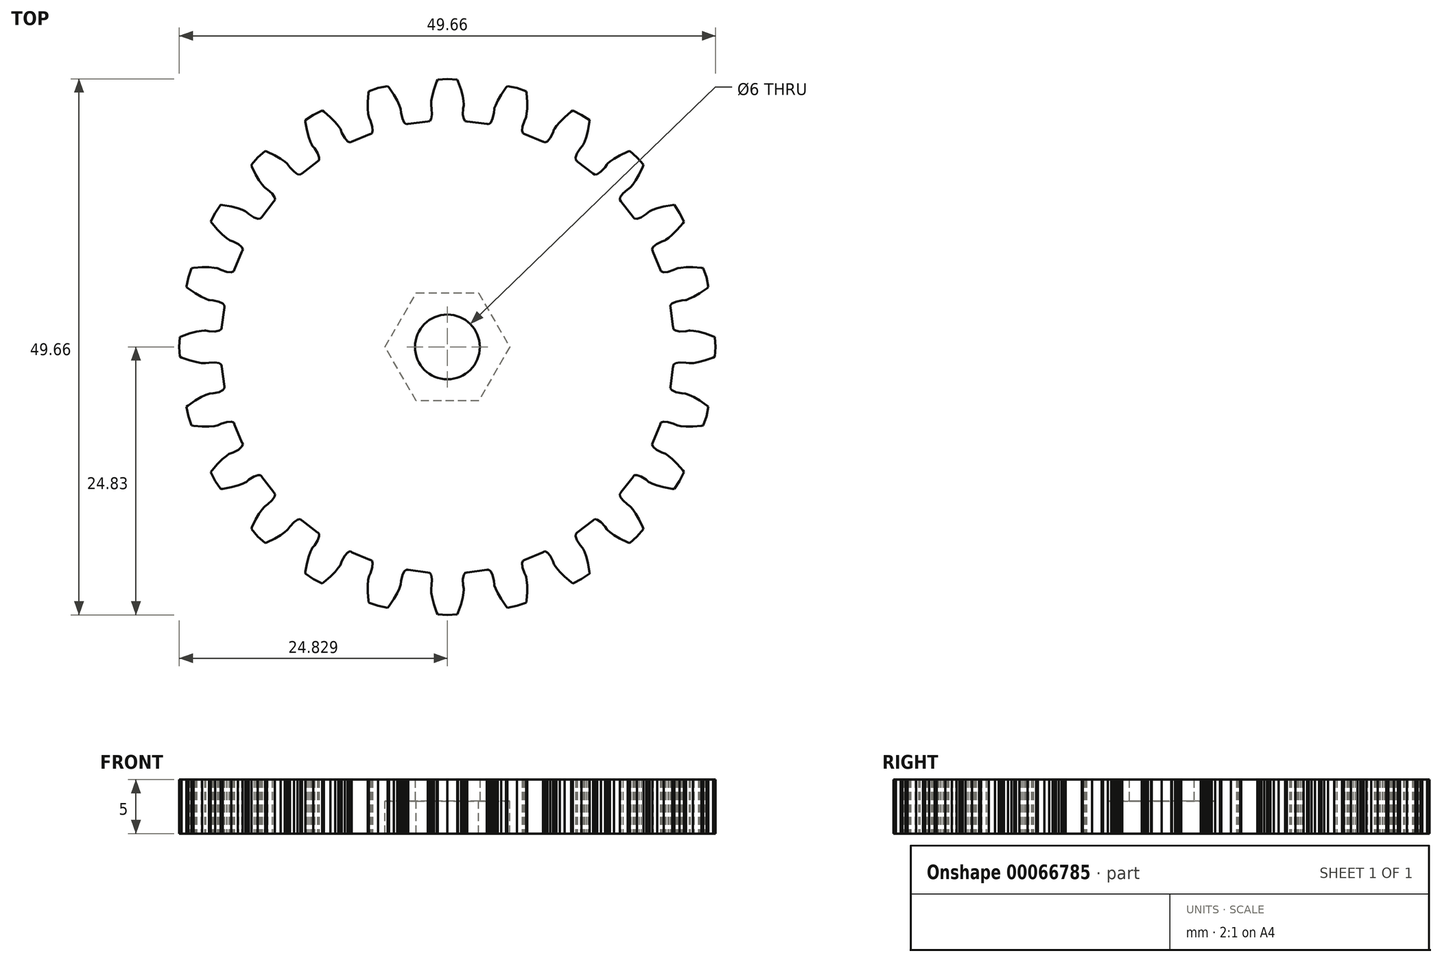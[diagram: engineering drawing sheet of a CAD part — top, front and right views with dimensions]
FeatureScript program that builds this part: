
annotation { "Feature Type Name" : "Feature", "Feature Type Description" : "" }
export const myFeature = defineFeature(function(context is Context, id is Id, definition is map)
    precondition{}
    {
        {
            var Q0;
            Q0=qCreatedBy(makeId("Top.planeOp"),FACE);
            var sketch = newSketch(context, id + "F0", { "sketchPlane" : qUnion([Q0])});
            skLineSegment(sketch, "E0", {"start": v(16.31, -7.28) * mm, "end": v(16.6, -6.43) * mm});
            skLineSegment(sketch, "E1", {"start": v(16.6, -6.43) * mm, "end": v(16.78, -5.54) * mm});
            skLineSegment(sketch, "E2", {"start": v(16.78, -5.54) * mm, "end": v(16.64, -5.42) * mm});
            skLineSegment(sketch, "E3", {"start": v(16.64, -5.42) * mm, "end": v(15.98, -4.96) * mm});
            skLineSegment(sketch, "E4", {"start": v(15.98, -4.96) * mm, "end": v(15.42, -4.65) * mm});
            skLineSegment(sketch, "E5", {"start": v(15.42, -4.65) * mm, "end": v(15, -4.45) * mm});
            skLineSegment(sketch, "E6", {"start": v(15, -4.45) * mm, "end": v(14.73, -4.36) * mm});
            skLineSegment(sketch, "E7", {"start": v(14.73, -4.36) * mm, "end": v(14.63, -4.33) * mm});
            skLineSegment(sketch, "E8", {"start": v(14.63, -4.33) * mm, "end": v(14.33, -4.3) * mm});
            skLineSegment(sketch, "E9", {"start": v(14.33, -4.3) * mm, "end": v(13.78, -4.18) * mm});
            skLineSegment(sketch, "E10", {"start": v(13.78, -4.18) * mm, "end": v(13.42, -4.01) * mm});
            skLineSegment(sketch, "E11", {"start": v(13.42, -4.01) * mm, "end": v(13.25, -3.83) * mm});
            skLineSegment(sketch, "E12", {"start": v(13.25, -3.83) * mm, "end": v(13.28, -3.66) * mm});
            skLineSegment(sketch, "E13", {"start": v(13.28, -3.66) * mm, "end": v(13.28, -3.64) * mm});
            skLineSegment(sketch, "E14", {"start": v(13.28, -3.64) * mm, "end": v(13.52, -1.83) * mm});
            skLineSegment(sketch, "E15", {"start": v(13.52, -1.83) * mm, "end": v(13.52, -1.81) * mm});
            skLineSegment(sketch, "E16", {"start": v(13.52, -1.81) * mm, "end": v(13.54, -1.64) * mm});
            skLineSegment(sketch, "E17", {"start": v(13.54, -1.64) * mm, "end": v(13.75, -1.5) * mm});
            skLineSegment(sketch, "E18", {"start": v(13.75, -1.5) * mm, "end": v(14.14, -1.44) * mm});
            skLineSegment(sketch, "E19", {"start": v(14.14, -1.44) * mm, "end": v(14.7, -1.46) * mm});
            skLineSegment(sketch, "E20", {"start": v(14.7, -1.46) * mm, "end": v(15, -1.51) * mm});
            skLineSegment(sketch, "E21", {"start": v(15, -1.51) * mm, "end": v(15.1, -1.52) * mm});
            skLineSegment(sketch, "E22", {"start": v(15.1, -1.52) * mm, "end": v(15.4, -1.5) * mm});
            skLineSegment(sketch, "E23", {"start": v(15.4, -1.5) * mm, "end": v(15.85, -1.41) * mm});
            skLineSegment(sketch, "E24", {"start": v(15.85, -1.41) * mm, "end": v(16.46, -1.25) * mm});
            skLineSegment(sketch, "E25", {"start": v(16.46, -1.25) * mm, "end": v(17.22, -0.98) * mm});
            skLineSegment(sketch, "E26", {"start": v(17.22, -0.98) * mm, "end": v(17.39, -0.9) * mm});
            skLineSegment(sketch, "E27", {"start": v(17.39, -0.9) * mm, "end": v(17.45, 0) * mm});
            skLineSegment(sketch, "E28", {"start": v(17.45, 0) * mm, "end": v(17.39, 0.9) * mm});
            skLineSegment(sketch, "E29", {"start": v(17.39, 0.9) * mm, "end": v(17.22, 0.98) * mm});
            skLineSegment(sketch, "E30", {"start": v(17.22, 0.98) * mm, "end": v(16.46, 1.25) * mm});
            skLineSegment(sketch, "E31", {"start": v(16.46, 1.25) * mm, "end": v(15.85, 1.41) * mm});
            skLineSegment(sketch, "E32", {"start": v(15.85, 1.41) * mm, "end": v(15.4, 1.5) * mm});
            skLineSegment(sketch, "E33", {"start": v(15.4, 1.5) * mm, "end": v(15.1, 1.52) * mm});
            skLineSegment(sketch, "E34", {"start": v(15.1, 1.52) * mm, "end": v(15, 1.51) * mm});
            skLineSegment(sketch, "E35", {"start": v(15, 1.51) * mm, "end": v(14.7, 1.46) * mm});
            skLineSegment(sketch, "E36", {"start": v(14.7, 1.46) * mm, "end": v(14.14, 1.44) * mm});
            skLineSegment(sketch, "E37", {"start": v(14.14, 1.44) * mm, "end": v(13.75, 1.5) * mm});
            skLineSegment(sketch, "E38", {"start": v(13.75, 1.5) * mm, "end": v(13.54, 1.64) * mm});
            skLineSegment(sketch, "E39", {"start": v(13.54, 1.64) * mm, "end": v(13.52, 1.81) * mm});
            skLineSegment(sketch, "E40", {"start": v(13.52, 1.81) * mm, "end": v(13.52, 1.83) * mm});
            skLineSegment(sketch, "E41", {"start": v(13.52, 1.83) * mm, "end": v(13.28, 3.64) * mm});
            skLineSegment(sketch, "E42", {"start": v(13.28, 3.64) * mm, "end": v(13.28, 3.66) * mm});
            skLineSegment(sketch, "E43", {"start": v(13.28, 3.66) * mm, "end": v(13.25, 3.83) * mm});
            skLineSegment(sketch, "E44", {"start": v(13.25, 3.83) * mm, "end": v(13.42, 4.01) * mm});
            skLineSegment(sketch, "E45", {"start": v(13.42, 4.01) * mm, "end": v(13.78, 4.18) * mm});
            skLineSegment(sketch, "E46", {"start": v(13.78, 4.18) * mm, "end": v(14.33, 4.3) * mm});
            skLineSegment(sketch, "E47", {"start": v(14.33, 4.3) * mm, "end": v(14.63, 4.33) * mm});
            skLineSegment(sketch, "E48", {"start": v(14.63, 4.33) * mm, "end": v(14.73, 4.36) * mm});
            skLineSegment(sketch, "E49", {"start": v(14.73, 4.36) * mm, "end": v(15, 4.45) * mm});
            skLineSegment(sketch, "E50", {"start": v(15, 4.45) * mm, "end": v(15.42, 4.65) * mm});
            skLineSegment(sketch, "E51", {"start": v(15.42, 4.65) * mm, "end": v(15.98, 4.96) * mm});
            skLineSegment(sketch, "E52", {"start": v(15.98, 4.96) * mm, "end": v(16.64, 5.42) * mm});
            skLineSegment(sketch, "E53", {"start": v(16.64, 5.42) * mm, "end": v(16.78, 5.54) * mm});
            skLineSegment(sketch, "E54", {"start": v(16.78, 5.54) * mm, "end": v(16.6, 6.43) * mm});
            skLineSegment(sketch, "E55", {"start": v(16.6, 6.43) * mm, "end": v(16.31, 7.28) * mm});
            skLineSegment(sketch, "E56", {"start": v(16.31, 7.28) * mm, "end": v(16.13, 7.31) * mm});
            skLineSegment(sketch, "E57", {"start": v(16.13, 7.31) * mm, "end": v(15.33, 7.38) * mm});
            skLineSegment(sketch, "E58", {"start": v(15.33, 7.38) * mm, "end": v(14.7, 7.38) * mm});
            skLineSegment(sketch, "E59", {"start": v(14.7, 7.38) * mm, "end": v(14.23, 7.33) * mm});
            skLineSegment(sketch, "E60", {"start": v(14.23, 7.33) * mm, "end": v(13.94, 7.28) * mm});
            skLineSegment(sketch, "E61", {"start": v(13.94, 7.28) * mm, "end": v(13.85, 7.26) * mm});
            skLineSegment(sketch, "E62", {"start": v(13.85, 7.26) * mm, "end": v(13.57, 7.12) * mm});
            skLineSegment(sketch, "E63", {"start": v(13.57, 7.12) * mm, "end": v(13.04, 6.96) * mm});
            skLineSegment(sketch, "E64", {"start": v(13.04, 6.96) * mm, "end": v(12.64, 6.93) * mm});
            skLineSegment(sketch, "E65", {"start": v(12.64, 6.93) * mm, "end": v(12.4, 7) * mm});
            skLineSegment(sketch, "E66", {"start": v(12.4, 7) * mm, "end": v(12.34, 7.16) * mm});
            skLineSegment(sketch, "E67", {"start": v(12.34, 7.16) * mm, "end": v(12.33, 7.18) * mm});
            skLineSegment(sketch, "E68", {"start": v(12.33, 7.18) * mm, "end": v(11.63, 8.87) * mm});
            skLineSegment(sketch, "E69", {"start": v(11.63, 8.87) * mm, "end": v(11.62, 8.88) * mm});
            skLineSegment(sketch, "E70", {"start": v(11.62, 8.88) * mm, "end": v(11.56, 9.04) * mm});
            skLineSegment(sketch, "E71", {"start": v(11.56, 9.04) * mm, "end": v(11.67, 9.26) * mm});
            skLineSegment(sketch, "E72", {"start": v(11.67, 9.26) * mm, "end": v(11.98, 9.52) * mm});
            skLineSegment(sketch, "E73", {"start": v(11.98, 9.52) * mm, "end": v(12.47, 9.78) * mm});
            skLineSegment(sketch, "E74", {"start": v(12.47, 9.78) * mm, "end": v(12.76, 9.88) * mm});
            skLineSegment(sketch, "E75", {"start": v(12.76, 9.88) * mm, "end": v(12.85, 9.93) * mm});
            skLineSegment(sketch, "E76", {"start": v(12.85, 9.93) * mm, "end": v(13.09, 10.1) * mm});
            skLineSegment(sketch, "E77", {"start": v(13.09, 10.1) * mm, "end": v(13.44, 10.4) * mm});
            skLineSegment(sketch, "E78", {"start": v(13.44, 10.4) * mm, "end": v(13.9, 10.84) * mm});
            skLineSegment(sketch, "E79", {"start": v(13.9, 10.84) * mm, "end": v(14.42, 11.45) * mm});
            skLineSegment(sketch, "E80", {"start": v(14.42, 11.45) * mm, "end": v(14.52, 11.6) * mm});
            skLineSegment(sketch, "E81", {"start": v(14.52, 11.6) * mm, "end": v(14.12, 12.41) * mm});
            skLineSegment(sketch, "E82", {"start": v(14.12, 12.41) * mm, "end": v(13.62, 13.17) * mm});
            skLineSegment(sketch, "E83", {"start": v(13.62, 13.17) * mm, "end": v(13.44, 13.15) * mm});
            skLineSegment(sketch, "E84", {"start": v(13.44, 13.15) * mm, "end": v(12.64, 13) * mm});
            skLineSegment(sketch, "E85", {"start": v(12.64, 13) * mm, "end": v(12.03, 12.84) * mm});
            skLineSegment(sketch, "E86", {"start": v(12.03, 12.84) * mm, "end": v(11.6, 12.68) * mm});
            skLineSegment(sketch, "E87", {"start": v(11.6, 12.68) * mm, "end": v(11.33, 12.55) * mm});
            skLineSegment(sketch, "E88", {"start": v(11.33, 12.55) * mm, "end": v(11.25, 12.5) * mm});
            skLineSegment(sketch, "E89", {"start": v(11.25, 12.5) * mm, "end": v(11.01, 12.3) * mm});
            skLineSegment(sketch, "E90", {"start": v(11.01, 12.3) * mm, "end": v(10.54, 12) * mm});
            skLineSegment(sketch, "E91", {"start": v(10.54, 12) * mm, "end": v(10.17, 11.87) * mm});
            skLineSegment(sketch, "E92", {"start": v(10.17, 11.87) * mm, "end": v(9.92, 11.88) * mm});
            skLineSegment(sketch, "E93", {"start": v(9.92, 11.88) * mm, "end": v(9.81, 12.02) * mm});
            skLineSegment(sketch, "E94", {"start": v(9.81, 12.02) * mm, "end": v(9.8, 12.03) * mm});
            skLineSegment(sketch, "E95", {"start": v(9.8, 12.03) * mm, "end": v(8.69, 13.48) * mm});
            skLineSegment(sketch, "E96", {"start": v(8.69, 13.48) * mm, "end": v(8.68, 13.5) * mm});
            skLineSegment(sketch, "E97", {"start": v(8.68, 13.5) * mm, "end": v(8.58, 13.63) * mm});
            skLineSegment(sketch, "E98", {"start": v(8.58, 13.63) * mm, "end": v(8.63, 13.88) * mm});
            skLineSegment(sketch, "E99", {"start": v(8.63, 13.88) * mm, "end": v(8.85, 14.2) * mm});
            skLineSegment(sketch, "E100", {"start": v(8.85, 14.2) * mm, "end": v(9.26, 14.58) * mm});
            skLineSegment(sketch, "E101", {"start": v(9.26, 14.58) * mm, "end": v(9.52, 14.76) * mm});
            skLineSegment(sketch, "E102", {"start": v(9.52, 14.76) * mm, "end": v(9.59, 14.83) * mm});
            skLineSegment(sketch, "E103", {"start": v(9.59, 14.83) * mm, "end": v(9.78, 15.05) * mm});
            skLineSegment(sketch, "E104", {"start": v(9.78, 15.05) * mm, "end": v(10.05, 15.43) * mm});
            skLineSegment(sketch, "E105", {"start": v(10.05, 15.43) * mm, "end": v(10.37, 15.98) * mm});
            skLineSegment(sketch, "E106", {"start": v(10.37, 15.98) * mm, "end": v(10.7, 16.7) * mm});
            skLineSegment(sketch, "E107", {"start": v(10.7, 16.7) * mm, "end": v(10.77, 16.88) * mm});
            skLineSegment(sketch, "E108", {"start": v(10.77, 16.88) * mm, "end": v(10.18, 17.56) * mm});
            skLineSegment(sketch, "E109", {"start": v(10.18, 17.56) * mm, "end": v(9.5, 18.15) * mm});
            skLineSegment(sketch, "E110", {"start": v(9.5, 18.15) * mm, "end": v(9.32, 18.1) * mm});
            skLineSegment(sketch, "E111", {"start": v(9.32, 18.1) * mm, "end": v(8.6, 17.75) * mm});
            skLineSegment(sketch, "E112", {"start": v(8.6, 17.75) * mm, "end": v(8.05, 17.43) * mm});
            skLineSegment(sketch, "E113", {"start": v(8.05, 17.43) * mm, "end": v(7.67, 17.16) * mm});
            skLineSegment(sketch, "E114", {"start": v(7.67, 17.16) * mm, "end": v(7.44, 16.97) * mm});
            skLineSegment(sketch, "E115", {"start": v(7.44, 16.97) * mm, "end": v(7.38, 16.9) * mm});
            skLineSegment(sketch, "E116", {"start": v(7.38, 16.9) * mm, "end": v(7.2, 16.65) * mm});
            skLineSegment(sketch, "E117", {"start": v(7.2, 16.65) * mm, "end": v(6.82, 16.23) * mm});
            skLineSegment(sketch, "E118", {"start": v(6.82, 16.23) * mm, "end": v(6.5, 16) * mm});
            skLineSegment(sketch, "E119", {"start": v(6.5, 16) * mm, "end": v(6.25, 15.96) * mm});
            skLineSegment(sketch, "E120", {"start": v(6.25, 15.96) * mm, "end": v(6.12, 16.06) * mm});
            skLineSegment(sketch, "E121", {"start": v(6.12, 16.06) * mm, "end": v(6.1, 16.07) * mm});
            skLineSegment(sketch, "E122", {"start": v(6.1, 16.07) * mm, "end": v(4.65, 17.18) * mm});
            skLineSegment(sketch, "E123", {"start": v(4.65, 17.18) * mm, "end": v(4.64, 17.2) * mm});
            skLineSegment(sketch, "E124", {"start": v(4.64, 17.2) * mm, "end": v(4.5, 17.3) * mm});
            skLineSegment(sketch, "E125", {"start": v(4.5, 17.3) * mm, "end": v(4.5, 17.55) * mm});
            skLineSegment(sketch, "E126", {"start": v(4.5, 17.55) * mm, "end": v(4.62, 17.92) * mm});
            skLineSegment(sketch, "E127", {"start": v(4.62, 17.92) * mm, "end": v(4.92, 18.4) * mm});
            skLineSegment(sketch, "E128", {"start": v(4.92, 18.4) * mm, "end": v(5.12, 18.63) * mm});
            skLineSegment(sketch, "E129", {"start": v(5.12, 18.63) * mm, "end": v(5.17, 18.71) * mm});
            skLineSegment(sketch, "E130", {"start": v(5.17, 18.71) * mm, "end": v(5.3, 18.98) * mm});
            skLineSegment(sketch, "E131", {"start": v(5.3, 18.98) * mm, "end": v(5.46, 19.41) * mm});
            skLineSegment(sketch, "E132", {"start": v(5.46, 19.41) * mm, "end": v(5.63, 20.02) * mm});
            skLineSegment(sketch, "E133", {"start": v(5.63, 20.02) * mm, "end": v(5.77, 20.82) * mm});
            skLineSegment(sketch, "E134", {"start": v(5.77, 20.82) * mm, "end": v(5.79, 21) * mm});
            skLineSegment(sketch, "E135", {"start": v(5.79, 21) * mm, "end": v(5.03, 21.5) * mm});
            skLineSegment(sketch, "E136", {"start": v(5.03, 21.5) * mm, "end": v(4.22, 21.9) * mm});
            skLineSegment(sketch, "E137", {"start": v(4.22, 21.9) * mm, "end": v(4.07, 21.8) * mm});
            skLineSegment(sketch, "E138", {"start": v(4.07, 21.8) * mm, "end": v(3.46, 21.28) * mm});
            skLineSegment(sketch, "E139", {"start": v(3.46, 21.28) * mm, "end": v(3.01, 20.83) * mm});
            skLineSegment(sketch, "E140", {"start": v(3.01, 20.83) * mm, "end": v(2.71, 20.47) * mm});
            skLineSegment(sketch, "E141", {"start": v(2.71, 20.47) * mm, "end": v(2.55, 20.23) * mm});
            skLineSegment(sketch, "E142", {"start": v(2.55, 20.23) * mm, "end": v(2.5, 20.14) * mm});
            skLineSegment(sketch, "E143", {"start": v(2.5, 20.14) * mm, "end": v(2.4, 19.85) * mm});
            skLineSegment(sketch, "E144", {"start": v(2.4, 19.85) * mm, "end": v(2.14, 19.36) * mm});
            skLineSegment(sketch, "E145", {"start": v(2.14, 19.36) * mm, "end": v(1.88, 19.06) * mm});
            skLineSegment(sketch, "E146", {"start": v(1.88, 19.06) * mm, "end": v(1.66, 18.94) * mm});
            skLineSegment(sketch, "E147", {"start": v(1.66, 18.94) * mm, "end": v(1.5, 19) * mm});
            skLineSegment(sketch, "E148", {"start": v(1.5, 19) * mm, "end": v(1.48, 19.01) * mm});
            skLineSegment(sketch, "E149", {"start": v(1.48, 19.01) * mm, "end": v(-0.2, 19.71) * mm});
            skLineSegment(sketch, "E150", {"start": v(-0.2, 19.71) * mm, "end": v(-0.22, 19.72) * mm});
            skLineSegment(sketch, "E151", {"start": v(-0.22, 19.72) * mm, "end": v(-0.38, 19.78) * mm});
            skLineSegment(sketch, "E152", {"start": v(-0.38, 19.78) * mm, "end": v(-0.45, 20.02) * mm});
            skLineSegment(sketch, "E153", {"start": v(-0.45, 20.02) * mm, "end": v(-0.42, 20.42) * mm});
            skLineSegment(sketch, "E154", {"start": v(-0.42, 20.42) * mm, "end": v(-0.26, 20.95) * mm});
            skLineSegment(sketch, "E155", {"start": v(-0.26, 20.95) * mm, "end": v(-0.12, 21.23) * mm});
            skLineSegment(sketch, "E156", {"start": v(-0.12, 21.23) * mm, "end": v(-0.1, 21.32) * mm});
            skLineSegment(sketch, "E157", {"start": v(-0.1, 21.32) * mm, "end": v(-0.05, 21.61) * mm});
            skLineSegment(sketch, "E158", {"start": v(-0.05, 21.61) * mm, "end": v(0, 22.07) * mm});
            skLineSegment(sketch, "E159", {"start": v(0, 22.07) * mm, "end": v(0, 22.7) * mm});
            skLineSegment(sketch, "E160", {"start": v(0, 22.7) * mm, "end": v(-0.07, 23.51) * mm});
            skLineSegment(sketch, "E161", {"start": v(-0.07, 23.51) * mm, "end": v(-0.1, 23.7) * mm});
            skLineSegment(sketch, "E162", {"start": v(-0.1, 23.7) * mm, "end": v(-0.95, 23.98) * mm});
            skLineSegment(sketch, "E163", {"start": v(-0.95, 23.98) * mm, "end": v(-1.84, 24.16) * mm});
            skLineSegment(sketch, "E164", {"start": v(-1.84, 24.16) * mm, "end": v(-1.96, 24.02) * mm});
            skLineSegment(sketch, "E165", {"start": v(-1.96, 24.02) * mm, "end": v(-2.42, 23.36) * mm});
            skLineSegment(sketch, "E166", {"start": v(-2.42, 23.36) * mm, "end": v(-2.73, 22.8) * mm});
            skLineSegment(sketch, "E167", {"start": v(-2.73, 22.8) * mm, "end": v(-2.93, 22.38) * mm});
            skLineSegment(sketch, "E168", {"start": v(-2.93, 22.38) * mm, "end": v(-3.03, 22.1) * mm});
            skLineSegment(sketch, "E169", {"start": v(-3.03, 22.1) * mm, "end": v(-3.05, 22.01) * mm});
            skLineSegment(sketch, "E170", {"start": v(-3.05, 22.01) * mm, "end": v(-3.08, 21.7) * mm});
            skLineSegment(sketch, "E171", {"start": v(-3.08, 21.7) * mm, "end": v(-3.2, 21.16) * mm});
            skLineSegment(sketch, "E172", {"start": v(-3.2, 21.16) * mm, "end": v(-3.37, 20.8) * mm});
            skLineSegment(sketch, "E173", {"start": v(-3.37, 20.8) * mm, "end": v(-3.55, 20.64) * mm});
            skLineSegment(sketch, "E174", {"start": v(-3.55, 20.64) * mm, "end": v(-3.72, 20.66) * mm});
            skLineSegment(sketch, "E175", {"start": v(-3.72, 20.66) * mm, "end": v(-3.74, 20.66) * mm});
            skLineSegment(sketch, "E176", {"start": v(-3.74, 20.66) * mm, "end": v(-5.55, 20.9) * mm});
            skLineSegment(sketch, "E177", {"start": v(-5.55, 20.9) * mm, "end": v(-5.57, 20.9) * mm});
            skLineSegment(sketch, "E178", {"start": v(-5.57, 20.9) * mm, "end": v(-5.74, 20.92) * mm});
            skLineSegment(sketch, "E179", {"start": v(-5.74, 20.92) * mm, "end": v(-5.87, 21.13) * mm});
            skLineSegment(sketch, "E180", {"start": v(-5.87, 21.13) * mm, "end": v(-5.94, 21.52) * mm});
            skLineSegment(sketch, "E181", {"start": v(-5.94, 21.52) * mm, "end": v(-5.92, 22.08) * mm});
            skLineSegment(sketch, "E182", {"start": v(-5.92, 22.08) * mm, "end": v(-5.87, 22.38) * mm});
            skLineSegment(sketch, "E183", {"start": v(-5.87, 22.38) * mm, "end": v(-5.87, 22.48) * mm});
            skLineSegment(sketch, "E184", {"start": v(-5.87, 22.48) * mm, "end": v(-5.89, 22.77) * mm});
            skLineSegment(sketch, "E185", {"start": v(-5.89, 22.77) * mm, "end": v(-5.97, 23.23) * mm});
            skLineSegment(sketch, "E186", {"start": v(-5.97, 23.23) * mm, "end": v(-6.13, 23.85) * mm});
            skLineSegment(sketch, "E187", {"start": v(-6.13, 23.85) * mm, "end": v(-6.4, 24.6) * mm});
            skLineSegment(sketch, "E188", {"start": v(-6.4, 24.6) * mm, "end": v(-6.48, 24.77) * mm});
            skLineSegment(sketch, "E189", {"start": v(-6.48, 24.77) * mm, "end": v(-7.38, 24.83) * mm});
            skLineSegment(sketch, "E190", {"start": v(-7.38, 24.83) * mm, "end": v(-8.28, 24.77) * mm});
            skLineSegment(sketch, "E191", {"start": v(-8.28, 24.77) * mm, "end": v(-8.36, 24.6) * mm});
            skLineSegment(sketch, "E192", {"start": v(-8.36, 24.6) * mm, "end": v(-8.63, 23.85) * mm});
            skLineSegment(sketch, "E193", {"start": v(-8.63, 23.85) * mm, "end": v(-8.8, 23.23) * mm});
            skLineSegment(sketch, "E194", {"start": v(-8.8, 23.23) * mm, "end": v(-8.87, 22.77) * mm});
            skLineSegment(sketch, "E195", {"start": v(-8.87, 22.77) * mm, "end": v(-8.9, 22.48) * mm});
            skLineSegment(sketch, "E196", {"start": v(-8.9, 22.48) * mm, "end": v(-8.9, 22.38) * mm});
            skLineSegment(sketch, "E197", {"start": v(-8.9, 22.38) * mm, "end": v(-8.84, 22.08) * mm});
            skLineSegment(sketch, "E198", {"start": v(-8.84, 22.08) * mm, "end": v(-8.82, 21.52) * mm});
            skLineSegment(sketch, "E199", {"start": v(-8.82, 21.52) * mm, "end": v(-8.89, 21.13) * mm});
            skLineSegment(sketch, "E200", {"start": v(-8.89, 21.13) * mm, "end": v(-9.02, 20.92) * mm});
            skLineSegment(sketch, "E201", {"start": v(-9.02, 20.92) * mm, "end": v(-9.2, 20.9) * mm});
            skLineSegment(sketch, "E202", {"start": v(-9.2, 20.9) * mm, "end": v(-9.2, 20.9) * mm});
            skLineSegment(sketch, "E203", {"start": v(-9.2, 20.9) * mm, "end": v(-11.02, 20.66) * mm});
            skLineSegment(sketch, "E204", {"start": v(-11.02, 20.66) * mm, "end": v(-11.04, 20.66) * mm});
            skLineSegment(sketch, "E205", {"start": v(-11.04, 20.66) * mm, "end": v(-11.2, 20.64) * mm});
            skLineSegment(sketch, "E206", {"start": v(-11.2, 20.64) * mm, "end": v(-11.4, 20.8) * mm});
            skLineSegment(sketch, "E207", {"start": v(-11.4, 20.8) * mm, "end": v(-11.56, 21.16) * mm});
            skLineSegment(sketch, "E208", {"start": v(-11.56, 21.16) * mm, "end": v(-11.69, 21.7) * mm});
            skLineSegment(sketch, "E209", {"start": v(-11.69, 21.7) * mm, "end": v(-11.71, 22.01) * mm});
            skLineSegment(sketch, "E210", {"start": v(-11.71, 22.01) * mm, "end": v(-11.74, 22.1) * mm});
            skLineSegment(sketch, "E211", {"start": v(-11.74, 22.1) * mm, "end": v(-11.84, 22.38) * mm});
            skLineSegment(sketch, "E212", {"start": v(-11.84, 22.38) * mm, "end": v(-12.03, 22.8) * mm});
            skLineSegment(sketch, "E213", {"start": v(-12.03, 22.8) * mm, "end": v(-12.34, 23.36) * mm});
            skLineSegment(sketch, "E214", {"start": v(-12.34, 23.36) * mm, "end": v(-12.8, 24.02) * mm});
            skLineSegment(sketch, "E215", {"start": v(-12.8, 24.02) * mm, "end": v(-12.92, 24.16) * mm});
            skLineSegment(sketch, "E216", {"start": v(-12.92, 24.16) * mm, "end": v(-13.8, 23.98) * mm});
            skLineSegment(sketch, "E217", {"start": v(-13.8, 23.98) * mm, "end": v(-14.66, 23.7) * mm});
            skLineSegment(sketch, "E218", {"start": v(-14.66, 23.7) * mm, "end": v(-14.7, 23.51) * mm});
            skLineSegment(sketch, "E219", {"start": v(-14.7, 23.51) * mm, "end": v(-14.76, 22.7) * mm});
            skLineSegment(sketch, "E220", {"start": v(-14.76, 22.7) * mm, "end": v(-14.76, 22.07) * mm});
            skLineSegment(sketch, "E221", {"start": v(-14.76, 22.07) * mm, "end": v(-14.72, 21.61) * mm});
            skLineSegment(sketch, "E222", {"start": v(-14.72, 21.61) * mm, "end": v(-14.66, 21.32) * mm});
            skLineSegment(sketch, "E223", {"start": v(-14.66, 21.32) * mm, "end": v(-14.64, 21.23) * mm});
            skLineSegment(sketch, "E224", {"start": v(-14.64, 21.23) * mm, "end": v(-14.5, 20.95) * mm});
            skLineSegment(sketch, "E225", {"start": v(-14.5, 20.95) * mm, "end": v(-14.34, 20.42) * mm});
            skLineSegment(sketch, "E226", {"start": v(-14.34, 20.42) * mm, "end": v(-14.3, 20.02) * mm});
            skLineSegment(sketch, "E227", {"start": v(-14.3, 20.02) * mm, "end": v(-14.38, 19.78) * mm});
            skLineSegment(sketch, "E228", {"start": v(-14.38, 19.78) * mm, "end": v(-14.54, 19.72) * mm});
            skLineSegment(sketch, "E229", {"start": v(-14.54, 19.72) * mm, "end": v(-14.56, 19.71) * mm});
            skLineSegment(sketch, "E230", {"start": v(-14.56, 19.71) * mm, "end": v(-16.25, 19.01) * mm});
            skLineSegment(sketch, "E231", {"start": v(-16.25, 19.01) * mm, "end": v(-16.26, 19) * mm});
            skLineSegment(sketch, "E232", {"start": v(-16.26, 19) * mm, "end": v(-16.42, 18.94) * mm});
            skLineSegment(sketch, "E233", {"start": v(-16.42, 18.94) * mm, "end": v(-16.64, 19.06) * mm});
            skLineSegment(sketch, "E234", {"start": v(-16.64, 19.06) * mm, "end": v(-16.9, 19.36) * mm});
            skLineSegment(sketch, "E235", {"start": v(-16.9, 19.36) * mm, "end": v(-17.16, 19.85) * mm});
            skLineSegment(sketch, "E236", {"start": v(-17.16, 19.85) * mm, "end": v(-17.26, 20.14) * mm});
            skLineSegment(sketch, "E237", {"start": v(-17.26, 20.14) * mm, "end": v(-17.3, 20.23) * mm});
            skLineSegment(sketch, "E238", {"start": v(-17.3, 20.23) * mm, "end": v(-17.48, 20.47) * mm});
            skLineSegment(sketch, "E239", {"start": v(-17.48, 20.47) * mm, "end": v(-17.77, 20.83) * mm});
            skLineSegment(sketch, "E240", {"start": v(-17.77, 20.83) * mm, "end": v(-18.22, 21.28) * mm});
            skLineSegment(sketch, "E241", {"start": v(-18.22, 21.28) * mm, "end": v(-18.83, 21.8) * mm});
            skLineSegment(sketch, "E242", {"start": v(-18.83, 21.8) * mm, "end": v(-18.98, 21.9) * mm});
            skLineSegment(sketch, "E243", {"start": v(-18.98, 21.9) * mm, "end": v(-19.8, 21.5) * mm});
            skLineSegment(sketch, "E244", {"start": v(-19.8, 21.5) * mm, "end": v(-20.55, 21) * mm});
            skLineSegment(sketch, "E245", {"start": v(-20.55, 21) * mm, "end": v(-20.53, 20.82) * mm});
            skLineSegment(sketch, "E246", {"start": v(-20.53, 20.82) * mm, "end": v(-20.39, 20.02) * mm});
            skLineSegment(sketch, "E247", {"start": v(-20.39, 20.02) * mm, "end": v(-20.22, 19.41) * mm});
            skLineSegment(sketch, "E248", {"start": v(-20.22, 19.41) * mm, "end": v(-20.06, 18.98) * mm});
            skLineSegment(sketch, "E249", {"start": v(-20.06, 18.98) * mm, "end": v(-19.93, 18.71) * mm});
            skLineSegment(sketch, "E250", {"start": v(-19.93, 18.71) * mm, "end": v(-19.88, 18.63) * mm});
            skLineSegment(sketch, "E251", {"start": v(-19.88, 18.63) * mm, "end": v(-19.69, 18.4) * mm});
            skLineSegment(sketch, "E252", {"start": v(-19.69, 18.4) * mm, "end": v(-19.39, 17.92) * mm});
            skLineSegment(sketch, "E253", {"start": v(-19.39, 17.92) * mm, "end": v(-19.25, 17.55) * mm});
            skLineSegment(sketch, "E254", {"start": v(-19.25, 17.55) * mm, "end": v(-19.27, 17.3) * mm});
            skLineSegment(sketch, "E255", {"start": v(-19.27, 17.3) * mm, "end": v(-19.4, 17.2) * mm});
            skLineSegment(sketch, "E256", {"start": v(-19.4, 17.2) * mm, "end": v(-19.41, 17.18) * mm});
            skLineSegment(sketch, "E257", {"start": v(-19.41, 17.18) * mm, "end": v(-20.87, 16.07) * mm});
            skLineSegment(sketch, "E258", {"start": v(-20.87, 16.07) * mm, "end": v(-20.88, 16.06) * mm});
            skLineSegment(sketch, "E259", {"start": v(-20.88, 16.06) * mm, "end": v(-21.01, 15.96) * mm});
            skLineSegment(sketch, "E260", {"start": v(-21.01, 15.96) * mm, "end": v(-21.26, 16) * mm});
            skLineSegment(sketch, "E261", {"start": v(-21.26, 16) * mm, "end": v(-21.58, 16.23) * mm});
            skLineSegment(sketch, "E262", {"start": v(-21.58, 16.23) * mm, "end": v(-21.96, 16.65) * mm});
            skLineSegment(sketch, "E263", {"start": v(-21.96, 16.65) * mm, "end": v(-22.14, 16.9) * mm});
            skLineSegment(sketch, "E264", {"start": v(-22.14, 16.9) * mm, "end": v(-22.2, 16.97) * mm});
            skLineSegment(sketch, "E265", {"start": v(-22.2, 16.97) * mm, "end": v(-22.43, 17.16) * mm});
            skLineSegment(sketch, "E266", {"start": v(-22.43, 17.16) * mm, "end": v(-22.8, 17.43) * mm});
            skLineSegment(sketch, "E267", {"start": v(-22.8, 17.43) * mm, "end": v(-23.36, 17.75) * mm});
            skLineSegment(sketch, "E268", {"start": v(-23.36, 17.75) * mm, "end": v(-24.09, 18.1) * mm});
            skLineSegment(sketch, "E269", {"start": v(-24.09, 18.1) * mm, "end": v(-24.26, 18.15) * mm});
            skLineSegment(sketch, "E270", {"start": v(-24.26, 18.15) * mm, "end": v(-24.94, 17.56) * mm});
            skLineSegment(sketch, "E271", {"start": v(-24.94, 17.56) * mm, "end": v(-25.53, 16.88) * mm});
            skLineSegment(sketch, "E272", {"start": v(-25.53, 16.88) * mm, "end": v(-25.47, 16.7) * mm});
            skLineSegment(sketch, "E273", {"start": v(-25.47, 16.7) * mm, "end": v(-25.13, 15.98) * mm});
            skLineSegment(sketch, "E274", {"start": v(-25.13, 15.98) * mm, "end": v(-24.8, 15.43) * mm});
            skLineSegment(sketch, "E275", {"start": v(-24.8, 15.43) * mm, "end": v(-24.54, 15.05) * mm});
            skLineSegment(sketch, "E276", {"start": v(-24.54, 15.05) * mm, "end": v(-24.35, 14.83) * mm});
            skLineSegment(sketch, "E277", {"start": v(-24.35, 14.83) * mm, "end": v(-24.28, 14.76) * mm});
            skLineSegment(sketch, "E278", {"start": v(-24.28, 14.76) * mm, "end": v(-24.03, 14.58) * mm});
            skLineSegment(sketch, "E279", {"start": v(-24.03, 14.58) * mm, "end": v(-23.62, 14.2) * mm});
            skLineSegment(sketch, "E280", {"start": v(-23.62, 14.2) * mm, "end": v(-23.4, 13.88) * mm});
            skLineSegment(sketch, "E281", {"start": v(-23.4, 13.88) * mm, "end": v(-23.34, 13.63) * mm});
            skLineSegment(sketch, "E282", {"start": v(-23.34, 13.63) * mm, "end": v(-23.44, 13.5) * mm});
            skLineSegment(sketch, "E283", {"start": v(-23.44, 13.5) * mm, "end": v(-23.45, 13.48) * mm});
            skLineSegment(sketch, "E284", {"start": v(-23.45, 13.48) * mm, "end": v(-24.57, 12.03) * mm});
            skLineSegment(sketch, "E285", {"start": v(-24.57, 12.03) * mm, "end": v(-24.57, 12.02) * mm});
            skLineSegment(sketch, "E286", {"start": v(-24.57, 12.02) * mm, "end": v(-24.68, 11.88) * mm});
            skLineSegment(sketch, "E287", {"start": v(-24.68, 11.88) * mm, "end": v(-24.93, 11.87) * mm});
            skLineSegment(sketch, "E288", {"start": v(-24.93, 11.87) * mm, "end": v(-25.3, 12) * mm});
            skLineSegment(sketch, "E289", {"start": v(-25.3, 12) * mm, "end": v(-25.77, 12.3) * mm});
            skLineSegment(sketch, "E290", {"start": v(-25.77, 12.3) * mm, "end": v(-26, 12.5) * mm});
            skLineSegment(sketch, "E291", {"start": v(-26, 12.5) * mm, "end": v(-26.1, 12.55) * mm});
            skLineSegment(sketch, "E292", {"start": v(-26.1, 12.55) * mm, "end": v(-26.36, 12.68) * mm});
            skLineSegment(sketch, "E293", {"start": v(-26.36, 12.68) * mm, "end": v(-26.8, 12.84) * mm});
            skLineSegment(sketch, "E294", {"start": v(-26.8, 12.84) * mm, "end": v(-27.4, 13) * mm});
            skLineSegment(sketch, "E295", {"start": v(-27.4, 13) * mm, "end": v(-28.2, 13.15) * mm});
            skLineSegment(sketch, "E296", {"start": v(-28.2, 13.15) * mm, "end": v(-28.38, 13.17) * mm});
            skLineSegment(sketch, "E297", {"start": v(-28.38, 13.17) * mm, "end": v(-28.88, 12.41) * mm});
            skLineSegment(sketch, "E298", {"start": v(-28.88, 12.41) * mm, "end": v(-29.28, 11.6) * mm});
            skLineSegment(sketch, "E299", {"start": v(-29.28, 11.6) * mm, "end": v(-29.18, 11.45) * mm});
            skLineSegment(sketch, "E300", {"start": v(-29.18, 11.45) * mm, "end": v(-28.66, 10.84) * mm});
            skLineSegment(sketch, "E301", {"start": v(-28.66, 10.84) * mm, "end": v(-28.2, 10.4) * mm});
            skLineSegment(sketch, "E302", {"start": v(-28.2, 10.4) * mm, "end": v(-27.85, 10.1) * mm});
            skLineSegment(sketch, "E303", {"start": v(-27.85, 10.1) * mm, "end": v(-27.6, 9.93) * mm});
            skLineSegment(sketch, "E304", {"start": v(-27.6, 9.93) * mm, "end": v(-27.52, 9.88) * mm});
            skLineSegment(sketch, "E305", {"start": v(-27.52, 9.88) * mm, "end": v(-27.23, 9.78) * mm});
            skLineSegment(sketch, "E306", {"start": v(-27.23, 9.78) * mm, "end": v(-26.74, 9.52) * mm});
            skLineSegment(sketch, "E307", {"start": v(-26.74, 9.52) * mm, "end": v(-26.44, 9.26) * mm});
            skLineSegment(sketch, "E308", {"start": v(-26.44, 9.26) * mm, "end": v(-26.32, 9.04) * mm});
            skLineSegment(sketch, "E309", {"start": v(-26.32, 9.04) * mm, "end": v(-26.39, 8.88) * mm});
            skLineSegment(sketch, "E310", {"start": v(-26.39, 8.88) * mm, "end": v(-26.4, 8.87) * mm});
            skLineSegment(sketch, "E311", {"start": v(-26.4, 8.87) * mm, "end": v(-27.1, 7.18) * mm});
            skLineSegment(sketch, "E312", {"start": v(-27.1, 7.18) * mm, "end": v(-27.1, 7.16) * mm});
            skLineSegment(sketch, "E313", {"start": v(-27.1, 7.16) * mm, "end": v(-27.17, 7) * mm});
            skLineSegment(sketch, "E314", {"start": v(-27.17, 7) * mm, "end": v(-27.4, 6.93) * mm});
            skLineSegment(sketch, "E315", {"start": v(-27.4, 6.93) * mm, "end": v(-27.8, 6.96) * mm});
            skLineSegment(sketch, "E316", {"start": v(-27.8, 6.96) * mm, "end": v(-28.33, 7.12) * mm});
            skLineSegment(sketch, "E317", {"start": v(-28.33, 7.12) * mm, "end": v(-28.61, 7.26) * mm});
            skLineSegment(sketch, "E318", {"start": v(-28.61, 7.26) * mm, "end": v(-28.7, 7.28) * mm});
            skLineSegment(sketch, "E319", {"start": v(-28.7, 7.28) * mm, "end": v(-29, 7.33) * mm});
            skLineSegment(sketch, "E320", {"start": v(-29, 7.33) * mm, "end": v(-29.46, 7.38) * mm});
            skLineSegment(sketch, "E321", {"start": v(-29.46, 7.38) * mm, "end": v(-30.09, 7.38) * mm});
            skLineSegment(sketch, "E322", {"start": v(-30.09, 7.38) * mm, "end": v(-30.9, 7.31) * mm});
            skLineSegment(sketch, "E323", {"start": v(-30.9, 7.31) * mm, "end": v(-31.07, 7.28) * mm});
            skLineSegment(sketch, "E324", {"start": v(-31.07, 7.28) * mm, "end": v(-31.36, 6.43) * mm});
            skLineSegment(sketch, "E325", {"start": v(-31.36, 6.43) * mm, "end": v(-31.54, 5.54) * mm});
            skLineSegment(sketch, "E326", {"start": v(-31.54, 5.54) * mm, "end": v(-31.4, 5.42) * mm});
            skLineSegment(sketch, "E327", {"start": v(-31.4, 5.42) * mm, "end": v(-30.74, 4.96) * mm});
            skLineSegment(sketch, "E328", {"start": v(-30.74, 4.96) * mm, "end": v(-30.19, 4.65) * mm});
            skLineSegment(sketch, "E329", {"start": v(-30.19, 4.65) * mm, "end": v(-29.77, 4.45) * mm});
            skLineSegment(sketch, "E330", {"start": v(-29.77, 4.45) * mm, "end": v(-29.49, 4.36) * mm});
            skLineSegment(sketch, "E331", {"start": v(-29.49, 4.36) * mm, "end": v(-29.4, 4.33) * mm});
            skLineSegment(sketch, "E332", {"start": v(-29.4, 4.33) * mm, "end": v(-29.09, 4.3) * mm});
            skLineSegment(sketch, "E333", {"start": v(-29.09, 4.3) * mm, "end": v(-28.54, 4.18) * mm});
            skLineSegment(sketch, "E334", {"start": v(-28.54, 4.18) * mm, "end": v(-28.18, 4.01) * mm});
            skLineSegment(sketch, "E335", {"start": v(-28.18, 4.01) * mm, "end": v(-28.02, 3.83) * mm});
            skLineSegment(sketch, "E336", {"start": v(-28.02, 3.83) * mm, "end": v(-28.04, 3.66) * mm});
            skLineSegment(sketch, "E337", {"start": v(-28.04, 3.66) * mm, "end": v(-28.04, 3.64) * mm});
            skLineSegment(sketch, "E338", {"start": v(-28.04, 3.64) * mm, "end": v(-28.28, 1.83) * mm});
            skLineSegment(sketch, "E339", {"start": v(-28.28, 1.83) * mm, "end": v(-28.28, 1.81) * mm});
            skLineSegment(sketch, "E340", {"start": v(-28.28, 1.81) * mm, "end": v(-28.3, 1.64) * mm});
            skLineSegment(sketch, "E341", {"start": v(-28.3, 1.64) * mm, "end": v(-28.51, 1.5) * mm});
            skLineSegment(sketch, "E342", {"start": v(-28.51, 1.5) * mm, "end": v(-28.9, 1.44) * mm});
            skLineSegment(sketch, "E343", {"start": v(-28.9, 1.44) * mm, "end": v(-29.46, 1.46) * mm});
            skLineSegment(sketch, "E344", {"start": v(-29.46, 1.46) * mm, "end": v(-29.76, 1.51) * mm});
            skLineSegment(sketch, "E345", {"start": v(-29.76, 1.51) * mm, "end": v(-29.86, 1.52) * mm});
            skLineSegment(sketch, "E346", {"start": v(-29.86, 1.52) * mm, "end": v(-30.16, 1.5) * mm});
            skLineSegment(sketch, "E347", {"start": v(-30.16, 1.5) * mm, "end": v(-30.61, 1.41) * mm});
            skLineSegment(sketch, "E348", {"start": v(-30.61, 1.41) * mm, "end": v(-31.23, 1.25) * mm});
            skLineSegment(sketch, "E349", {"start": v(-31.23, 1.25) * mm, "end": v(-31.98, 0.98) * mm});
            skLineSegment(sketch, "E350", {"start": v(-31.98, 0.98) * mm, "end": v(-32.15, 0.9) * mm});
            skLineSegment(sketch, "E351", {"start": v(-32.15, 0.9) * mm, "end": v(-32.2, 0) * mm});
            skLineSegment(sketch, "E352", {"start": v(-32.2, 0) * mm, "end": v(-32.15, -0.9) * mm});
            skLineSegment(sketch, "E353", {"start": v(-32.15, -0.9) * mm, "end": v(-31.98, -0.98) * mm});
            skLineSegment(sketch, "E354", {"start": v(-31.98, -0.98) * mm, "end": v(-31.23, -1.25) * mm});
            skLineSegment(sketch, "E355", {"start": v(-31.23, -1.25) * mm, "end": v(-30.61, -1.41) * mm});
            skLineSegment(sketch, "E356", {"start": v(-30.61, -1.41) * mm, "end": v(-30.16, -1.5) * mm});
            skLineSegment(sketch, "E357", {"start": v(-30.16, -1.5) * mm, "end": v(-29.86, -1.52) * mm});
            skLineSegment(sketch, "E358", {"start": v(-29.86, -1.52) * mm, "end": v(-29.76, -1.51) * mm});
            skLineSegment(sketch, "E359", {"start": v(-29.76, -1.51) * mm, "end": v(-29.46, -1.46) * mm});
            skLineSegment(sketch, "E360", {"start": v(-29.46, -1.46) * mm, "end": v(-28.9, -1.44) * mm});
            skLineSegment(sketch, "E361", {"start": v(-28.9, -1.44) * mm, "end": v(-28.51, -1.5) * mm});
            skLineSegment(sketch, "E362", {"start": v(-28.51, -1.5) * mm, "end": v(-28.3, -1.64) * mm});
            skLineSegment(sketch, "E363", {"start": v(-28.3, -1.64) * mm, "end": v(-28.28, -1.81) * mm});
            skLineSegment(sketch, "E364", {"start": v(-28.28, -1.81) * mm, "end": v(-28.28, -1.83) * mm});
            skLineSegment(sketch, "E365", {"start": v(-28.28, -1.83) * mm, "end": v(-28.04, -3.64) * mm});
            skLineSegment(sketch, "E366", {"start": v(-28.04, -3.64) * mm, "end": v(-28.04, -3.66) * mm});
            skLineSegment(sketch, "E367", {"start": v(-28.04, -3.66) * mm, "end": v(-28.02, -3.83) * mm});
            skLineSegment(sketch, "E368", {"start": v(-28.02, -3.83) * mm, "end": v(-28.18, -4.01) * mm});
            skLineSegment(sketch, "E369", {"start": v(-28.18, -4.01) * mm, "end": v(-28.54, -4.18) * mm});
            skLineSegment(sketch, "E370", {"start": v(-28.54, -4.18) * mm, "end": v(-29.09, -4.3) * mm});
            skLineSegment(sketch, "E371", {"start": v(-29.09, -4.3) * mm, "end": v(-29.4, -4.33) * mm});
            skLineSegment(sketch, "E372", {"start": v(-29.4, -4.33) * mm, "end": v(-29.49, -4.36) * mm});
            skLineSegment(sketch, "E373", {"start": v(-29.49, -4.36) * mm, "end": v(-29.77, -4.45) * mm});
            skLineSegment(sketch, "E374", {"start": v(-29.77, -4.45) * mm, "end": v(-30.19, -4.65) * mm});
            skLineSegment(sketch, "E375", {"start": v(-30.19, -4.65) * mm, "end": v(-30.74, -4.96) * mm});
            skLineSegment(sketch, "E376", {"start": v(-30.74, -4.96) * mm, "end": v(-31.4, -5.42) * mm});
            skLineSegment(sketch, "E377", {"start": v(-31.4, -5.42) * mm, "end": v(-31.54, -5.54) * mm});
            skLineSegment(sketch, "E378", {"start": v(-31.54, -5.54) * mm, "end": v(-31.36, -6.43) * mm});
            skLineSegment(sketch, "E379", {"start": v(-31.36, -6.43) * mm, "end": v(-31.07, -7.28) * mm});
            skLineSegment(sketch, "E380", {"start": v(-31.07, -7.28) * mm, "end": v(-30.9, -7.31) * mm});
            skLineSegment(sketch, "E381", {"start": v(-30.9, -7.31) * mm, "end": v(-30.09, -7.38) * mm});
            skLineSegment(sketch, "E382", {"start": v(-30.09, -7.38) * mm, "end": v(-29.46, -7.38) * mm});
            skLineSegment(sketch, "E383", {"start": v(-29.46, -7.38) * mm, "end": v(-29, -7.33) * mm});
            skLineSegment(sketch, "E384", {"start": v(-29, -7.33) * mm, "end": v(-28.7, -7.28) * mm});
            skLineSegment(sketch, "E385", {"start": v(-28.7, -7.28) * mm, "end": v(-28.61, -7.26) * mm});
            skLineSegment(sketch, "E386", {"start": v(-28.61, -7.26) * mm, "end": v(-28.33, -7.12) * mm});
            skLineSegment(sketch, "E387", {"start": v(-28.33, -7.12) * mm, "end": v(-27.8, -6.96) * mm});
            skLineSegment(sketch, "E388", {"start": v(-27.8, -6.96) * mm, "end": v(-27.4, -6.93) * mm});
            skLineSegment(sketch, "E389", {"start": v(-27.4, -6.93) * mm, "end": v(-27.17, -7) * mm});
            skLineSegment(sketch, "E390", {"start": v(-27.17, -7) * mm, "end": v(-27.1, -7.16) * mm});
            skLineSegment(sketch, "E391", {"start": v(-27.1, -7.16) * mm, "end": v(-27.1, -7.18) * mm});
            skLineSegment(sketch, "E392", {"start": v(-27.1, -7.18) * mm, "end": v(-26.4, -8.87) * mm});
            skLineSegment(sketch, "E393", {"start": v(-26.4, -8.87) * mm, "end": v(-26.39, -8.88) * mm});
            skLineSegment(sketch, "E394", {"start": v(-26.39, -8.88) * mm, "end": v(-26.32, -9.04) * mm});
            skLineSegment(sketch, "E395", {"start": v(-26.32, -9.04) * mm, "end": v(-26.44, -9.26) * mm});
            skLineSegment(sketch, "E396", {"start": v(-26.44, -9.26) * mm, "end": v(-26.74, -9.52) * mm});
            skLineSegment(sketch, "E397", {"start": v(-26.74, -9.52) * mm, "end": v(-27.23, -9.78) * mm});
            skLineSegment(sketch, "E398", {"start": v(-27.23, -9.78) * mm, "end": v(-27.52, -9.88) * mm});
            skLineSegment(sketch, "E399", {"start": v(-27.52, -9.88) * mm, "end": v(-27.6, -9.93) * mm});
            skLineSegment(sketch, "E400", {"start": v(-27.6, -9.93) * mm, "end": v(-27.85, -10.1) * mm});
            skLineSegment(sketch, "E401", {"start": v(-27.85, -10.1) * mm, "end": v(-28.2, -10.4) * mm});
            skLineSegment(sketch, "E402", {"start": v(-28.2, -10.4) * mm, "end": v(-28.66, -10.84) * mm});
            skLineSegment(sketch, "E403", {"start": v(-28.66, -10.84) * mm, "end": v(-29.18, -11.45) * mm});
            skLineSegment(sketch, "E404", {"start": v(-29.18, -11.45) * mm, "end": v(-29.28, -11.6) * mm});
            skLineSegment(sketch, "E405", {"start": v(-29.28, -11.6) * mm, "end": v(-28.88, -12.41) * mm});
            skLineSegment(sketch, "E406", {"start": v(-28.88, -12.41) * mm, "end": v(-28.38, -13.17) * mm});
            skLineSegment(sketch, "E407", {"start": v(-28.38, -13.17) * mm, "end": v(-28.2, -13.15) * mm});
            skLineSegment(sketch, "E408", {"start": v(-28.2, -13.15) * mm, "end": v(-27.4, -13) * mm});
            skLineSegment(sketch, "E409", {"start": v(-27.4, -13) * mm, "end": v(-26.8, -12.84) * mm});
            skLineSegment(sketch, "E410", {"start": v(-26.8, -12.84) * mm, "end": v(-26.36, -12.68) * mm});
            skLineSegment(sketch, "E411", {"start": v(-26.36, -12.68) * mm, "end": v(-26.1, -12.55) * mm});
            skLineSegment(sketch, "E412", {"start": v(-26.1, -12.55) * mm, "end": v(-26, -12.5) * mm});
            skLineSegment(sketch, "E413", {"start": v(-26, -12.5) * mm, "end": v(-25.77, -12.3) * mm});
            skLineSegment(sketch, "E414", {"start": v(-25.77, -12.3) * mm, "end": v(-25.3, -12) * mm});
            skLineSegment(sketch, "E415", {"start": v(-25.3, -12) * mm, "end": v(-24.93, -11.87) * mm});
            skLineSegment(sketch, "E416", {"start": v(-24.93, -11.87) * mm, "end": v(-24.68, -11.88) * mm});
            skLineSegment(sketch, "E417", {"start": v(-24.68, -11.88) * mm, "end": v(-24.57, -12.02) * mm});
            skLineSegment(sketch, "E418", {"start": v(-24.57, -12.02) * mm, "end": v(-24.57, -12.03) * mm});
            skLineSegment(sketch, "E419", {"start": v(-24.57, -12.03) * mm, "end": v(-23.45, -13.48) * mm});
            skLineSegment(sketch, "E420", {"start": v(-23.45, -13.48) * mm, "end": v(-23.44, -13.5) * mm});
            skLineSegment(sketch, "E421", {"start": v(-23.44, -13.5) * mm, "end": v(-23.34, -13.63) * mm});
            skLineSegment(sketch, "E422", {"start": v(-23.34, -13.63) * mm, "end": v(-23.4, -13.88) * mm});
            skLineSegment(sketch, "E423", {"start": v(-23.4, -13.88) * mm, "end": v(-23.62, -14.2) * mm});
            skLineSegment(sketch, "E424", {"start": v(-23.62, -14.2) * mm, "end": v(-24.03, -14.58) * mm});
            skLineSegment(sketch, "E425", {"start": v(-24.03, -14.58) * mm, "end": v(-24.28, -14.76) * mm});
            skLineSegment(sketch, "E426", {"start": v(-24.28, -14.76) * mm, "end": v(-24.35, -14.83) * mm});
            skLineSegment(sketch, "E427", {"start": v(-24.35, -14.83) * mm, "end": v(-24.54, -15.05) * mm});
            skLineSegment(sketch, "E428", {"start": v(-24.54, -15.05) * mm, "end": v(-24.8, -15.43) * mm});
            skLineSegment(sketch, "E429", {"start": v(-24.8, -15.43) * mm, "end": v(-25.13, -15.98) * mm});
            skLineSegment(sketch, "E430", {"start": v(-25.13, -15.98) * mm, "end": v(-25.47, -16.7) * mm});
            skLineSegment(sketch, "E431", {"start": v(-25.47, -16.7) * mm, "end": v(-25.53, -16.88) * mm});
            skLineSegment(sketch, "E432", {"start": v(-25.53, -16.88) * mm, "end": v(-24.94, -17.56) * mm});
            skLineSegment(sketch, "E433", {"start": v(-24.94, -17.56) * mm, "end": v(-24.26, -18.15) * mm});
            skLineSegment(sketch, "E434", {"start": v(-24.26, -18.15) * mm, "end": v(-24.09, -18.1) * mm});
            skLineSegment(sketch, "E435", {"start": v(-24.09, -18.1) * mm, "end": v(-23.36, -17.75) * mm});
            skLineSegment(sketch, "E436", {"start": v(-23.36, -17.75) * mm, "end": v(-22.8, -17.43) * mm});
            skLineSegment(sketch, "E437", {"start": v(-22.8, -17.43) * mm, "end": v(-22.43, -17.16) * mm});
            skLineSegment(sketch, "E438", {"start": v(-22.43, -17.16) * mm, "end": v(-22.2, -16.97) * mm});
            skLineSegment(sketch, "E439", {"start": v(-22.2, -16.97) * mm, "end": v(-22.14, -16.9) * mm});
            skLineSegment(sketch, "E440", {"start": v(-22.14, -16.9) * mm, "end": v(-21.96, -16.65) * mm});
            skLineSegment(sketch, "E441", {"start": v(-21.96, -16.65) * mm, "end": v(-21.58, -16.23) * mm});
            skLineSegment(sketch, "E442", {"start": v(-21.58, -16.23) * mm, "end": v(-21.26, -16) * mm});
            skLineSegment(sketch, "E443", {"start": v(-21.26, -16) * mm, "end": v(-21.01, -15.96) * mm});
            skLineSegment(sketch, "E444", {"start": v(-21.01, -15.96) * mm, "end": v(-20.88, -16.06) * mm});
            skLineSegment(sketch, "E445", {"start": v(-20.88, -16.06) * mm, "end": v(-20.87, -16.07) * mm});
            skLineSegment(sketch, "E446", {"start": v(-20.87, -16.07) * mm, "end": v(-19.41, -17.18) * mm});
            skLineSegment(sketch, "E447", {"start": v(-19.41, -17.18) * mm, "end": v(-19.4, -17.2) * mm});
            skLineSegment(sketch, "E448", {"start": v(-19.4, -17.2) * mm, "end": v(-19.27, -17.3) * mm});
            skLineSegment(sketch, "E449", {"start": v(-19.27, -17.3) * mm, "end": v(-19.25, -17.55) * mm});
            skLineSegment(sketch, "E450", {"start": v(-19.25, -17.55) * mm, "end": v(-19.39, -17.92) * mm});
            skLineSegment(sketch, "E451", {"start": v(-19.39, -17.92) * mm, "end": v(-19.69, -18.4) * mm});
            skLineSegment(sketch, "E452", {"start": v(-19.69, -18.4) * mm, "end": v(-19.88, -18.63) * mm});
            skLineSegment(sketch, "E453", {"start": v(-19.88, -18.63) * mm, "end": v(-19.93, -18.71) * mm});
            skLineSegment(sketch, "E454", {"start": v(-19.93, -18.71) * mm, "end": v(-20.06, -18.98) * mm});
            skLineSegment(sketch, "E455", {"start": v(-20.06, -18.98) * mm, "end": v(-20.22, -19.41) * mm});
            skLineSegment(sketch, "E456", {"start": v(-20.22, -19.41) * mm, "end": v(-20.39, -20.02) * mm});
            skLineSegment(sketch, "E457", {"start": v(-20.39, -20.02) * mm, "end": v(-20.53, -20.82) * mm});
            skLineSegment(sketch, "E458", {"start": v(-20.53, -20.82) * mm, "end": v(-20.55, -21) * mm});
            skLineSegment(sketch, "E459", {"start": v(-20.55, -21) * mm, "end": v(-19.8, -21.5) * mm});
            skLineSegment(sketch, "E460", {"start": v(-19.8, -21.5) * mm, "end": v(-18.98, -21.9) * mm});
            skLineSegment(sketch, "E461", {"start": v(-18.98, -21.9) * mm, "end": v(-18.83, -21.8) * mm});
            skLineSegment(sketch, "E462", {"start": v(-18.83, -21.8) * mm, "end": v(-18.22, -21.28) * mm});
            skLineSegment(sketch, "E463", {"start": v(-18.22, -21.28) * mm, "end": v(-17.77, -20.83) * mm});
            skLineSegment(sketch, "E464", {"start": v(-17.77, -20.83) * mm, "end": v(-17.48, -20.47) * mm});
            skLineSegment(sketch, "E465", {"start": v(-17.48, -20.47) * mm, "end": v(-17.3, -20.23) * mm});
            skLineSegment(sketch, "E466", {"start": v(-17.3, -20.23) * mm, "end": v(-17.26, -20.14) * mm});
            skLineSegment(sketch, "E467", {"start": v(-17.26, -20.14) * mm, "end": v(-17.16, -19.85) * mm});
            skLineSegment(sketch, "E468", {"start": v(-17.16, -19.85) * mm, "end": v(-16.9, -19.36) * mm});
            skLineSegment(sketch, "E469", {"start": v(-16.9, -19.36) * mm, "end": v(-16.64, -19.06) * mm});
            skLineSegment(sketch, "E470", {"start": v(-16.64, -19.06) * mm, "end": v(-16.42, -18.94) * mm});
            skLineSegment(sketch, "E471", {"start": v(-16.42, -18.94) * mm, "end": v(-16.26, -19) * mm});
            skLineSegment(sketch, "E472", {"start": v(-16.26, -19) * mm, "end": v(-16.25, -19.01) * mm});
            skLineSegment(sketch, "E473", {"start": v(-16.25, -19.01) * mm, "end": v(-14.56, -19.71) * mm});
            skLineSegment(sketch, "E474", {"start": v(-14.56, -19.71) * mm, "end": v(-14.54, -19.72) * mm});
            skLineSegment(sketch, "E475", {"start": v(-14.54, -19.72) * mm, "end": v(-14.38, -19.78) * mm});
            skLineSegment(sketch, "E476", {"start": v(-14.38, -19.78) * mm, "end": v(-14.3, -20.02) * mm});
            skLineSegment(sketch, "E477", {"start": v(-14.3, -20.02) * mm, "end": v(-14.34, -20.42) * mm});
            skLineSegment(sketch, "E478", {"start": v(-14.34, -20.42) * mm, "end": v(-14.5, -20.95) * mm});
            skLineSegment(sketch, "E479", {"start": v(-14.5, -20.95) * mm, "end": v(-14.64, -21.23) * mm});
            skLineSegment(sketch, "E480", {"start": v(-14.64, -21.23) * mm, "end": v(-14.66, -21.32) * mm});
            skLineSegment(sketch, "E481", {"start": v(-14.66, -21.32) * mm, "end": v(-14.72, -21.61) * mm});
            skLineSegment(sketch, "E482", {"start": v(-14.72, -21.61) * mm, "end": v(-14.76, -22.07) * mm});
            skLineSegment(sketch, "E483", {"start": v(-14.76, -22.07) * mm, "end": v(-14.76, -22.7) * mm});
            skLineSegment(sketch, "E484", {"start": v(-14.76, -22.7) * mm, "end": v(-14.7, -23.51) * mm});
            skLineSegment(sketch, "E485", {"start": v(-14.7, -23.51) * mm, "end": v(-14.66, -23.7) * mm});
            skLineSegment(sketch, "E486", {"start": v(-14.66, -23.7) * mm, "end": v(-13.8, -23.98) * mm});
            skLineSegment(sketch, "E487", {"start": v(-13.8, -23.98) * mm, "end": v(-12.92, -24.16) * mm});
            skLineSegment(sketch, "E488", {"start": v(-12.92, -24.16) * mm, "end": v(-12.8, -24.02) * mm});
            skLineSegment(sketch, "E489", {"start": v(-12.8, -24.02) * mm, "end": v(-12.34, -23.36) * mm});
            skLineSegment(sketch, "E490", {"start": v(-12.34, -23.36) * mm, "end": v(-12.03, -22.8) * mm});
            skLineSegment(sketch, "E491", {"start": v(-12.03, -22.8) * mm, "end": v(-11.84, -22.38) * mm});
            skLineSegment(sketch, "E492", {"start": v(-11.84, -22.38) * mm, "end": v(-11.74, -22.1) * mm});
            skLineSegment(sketch, "E493", {"start": v(-11.74, -22.1) * mm, "end": v(-11.71, -22.01) * mm});
            skLineSegment(sketch, "E494", {"start": v(-11.71, -22.01) * mm, "end": v(-11.69, -21.7) * mm});
            skLineSegment(sketch, "E495", {"start": v(-11.69, -21.7) * mm, "end": v(-11.56, -21.16) * mm});
            skLineSegment(sketch, "E496", {"start": v(-11.56, -21.16) * mm, "end": v(-11.4, -20.8) * mm});
            skLineSegment(sketch, "E497", {"start": v(-11.4, -20.8) * mm, "end": v(-11.2, -20.64) * mm});
            skLineSegment(sketch, "E498", {"start": v(-11.2, -20.64) * mm, "end": v(-11.04, -20.66) * mm});
            skLineSegment(sketch, "E499", {"start": v(-11.04, -20.66) * mm, "end": v(-11.02, -20.66) * mm});
            skLineSegment(sketch, "E500", {"start": v(-11.02, -20.66) * mm, "end": v(-9.2, -20.9) * mm});
            skLineSegment(sketch, "E501", {"start": v(-9.2, -20.9) * mm, "end": v(-9.2, -20.9) * mm});
            skLineSegment(sketch, "E502", {"start": v(-9.2, -20.9) * mm, "end": v(-9.02, -20.92) * mm});
            skLineSegment(sketch, "E503", {"start": v(-9.02, -20.92) * mm, "end": v(-8.89, -21.13) * mm});
            skLineSegment(sketch, "E504", {"start": v(-8.89, -21.13) * mm, "end": v(-8.82, -21.52) * mm});
            skLineSegment(sketch, "E505", {"start": v(-8.82, -21.52) * mm, "end": v(-8.84, -22.08) * mm});
            skLineSegment(sketch, "E506", {"start": v(-8.84, -22.08) * mm, "end": v(-8.9, -22.38) * mm});
            skLineSegment(sketch, "E507", {"start": v(-8.9, -22.38) * mm, "end": v(-8.9, -22.48) * mm});
            skLineSegment(sketch, "E508", {"start": v(-8.9, -22.48) * mm, "end": v(-8.87, -22.77) * mm});
            skLineSegment(sketch, "E509", {"start": v(-8.87, -22.77) * mm, "end": v(-8.8, -23.23) * mm});
            skLineSegment(sketch, "E510", {"start": v(-8.8, -23.23) * mm, "end": v(-8.63, -23.85) * mm});
            skLineSegment(sketch, "E511", {"start": v(-8.63, -23.85) * mm, "end": v(-8.36, -24.6) * mm});
            skLineSegment(sketch, "E512", {"start": v(-8.36, -24.6) * mm, "end": v(-8.28, -24.77) * mm});
            skLineSegment(sketch, "E513", {"start": v(-8.28, -24.77) * mm, "end": v(-7.38, -24.83) * mm});
            skLineSegment(sketch, "E514", {"start": v(-7.38, -24.83) * mm, "end": v(-6.48, -24.77) * mm});
            skLineSegment(sketch, "E515", {"start": v(-6.48, -24.77) * mm, "end": v(-6.4, -24.6) * mm});
            skLineSegment(sketch, "E516", {"start": v(-6.4, -24.6) * mm, "end": v(-6.13, -23.85) * mm});
            skLineSegment(sketch, "E517", {"start": v(-6.13, -23.85) * mm, "end": v(-5.97, -23.23) * mm});
            skLineSegment(sketch, "E518", {"start": v(-5.97, -23.23) * mm, "end": v(-5.89, -22.77) * mm});
            skLineSegment(sketch, "E519", {"start": v(-5.89, -22.77) * mm, "end": v(-5.87, -22.48) * mm});
            skLineSegment(sketch, "E520", {"start": v(-5.87, -22.48) * mm, "end": v(-5.87, -22.38) * mm});
            skLineSegment(sketch, "E521", {"start": v(-5.87, -22.38) * mm, "end": v(-5.92, -22.08) * mm});
            skLineSegment(sketch, "E522", {"start": v(-5.92, -22.08) * mm, "end": v(-5.94, -21.52) * mm});
            skLineSegment(sketch, "E523", {"start": v(-5.94, -21.52) * mm, "end": v(-5.87, -21.13) * mm});
            skLineSegment(sketch, "E524", {"start": v(-5.87, -21.13) * mm, "end": v(-5.74, -20.92) * mm});
            skLineSegment(sketch, "E525", {"start": v(-5.74, -20.92) * mm, "end": v(-5.57, -20.9) * mm});
            skLineSegment(sketch, "E526", {"start": v(-5.57, -20.9) * mm, "end": v(-5.55, -20.9) * mm});
            skLineSegment(sketch, "E527", {"start": v(-5.55, -20.9) * mm, "end": v(-3.74, -20.66) * mm});
            skLineSegment(sketch, "E528", {"start": v(-3.74, -20.66) * mm, "end": v(-3.72, -20.66) * mm});
            skLineSegment(sketch, "E529", {"start": v(-3.72, -20.66) * mm, "end": v(-3.55, -20.64) * mm});
            skLineSegment(sketch, "E530", {"start": v(-3.55, -20.64) * mm, "end": v(-3.37, -20.8) * mm});
            skLineSegment(sketch, "E531", {"start": v(-3.37, -20.8) * mm, "end": v(-3.2, -21.16) * mm});
            skLineSegment(sketch, "E532", {"start": v(-3.2, -21.16) * mm, "end": v(-3.08, -21.7) * mm});
            skLineSegment(sketch, "E533", {"start": v(-3.08, -21.7) * mm, "end": v(-3.05, -22.01) * mm});
            skLineSegment(sketch, "E534", {"start": v(-3.05, -22.01) * mm, "end": v(-3.03, -22.1) * mm});
            skLineSegment(sketch, "E535", {"start": v(-3.03, -22.1) * mm, "end": v(-2.93, -22.38) * mm});
            skLineSegment(sketch, "E536", {"start": v(-2.93, -22.38) * mm, "end": v(-2.73, -22.8) * mm});
            skLineSegment(sketch, "E537", {"start": v(-2.73, -22.8) * mm, "end": v(-2.42, -23.36) * mm});
            skLineSegment(sketch, "E538", {"start": v(-2.42, -23.36) * mm, "end": v(-1.96, -24.02) * mm});
            skLineSegment(sketch, "E539", {"start": v(-1.96, -24.02) * mm, "end": v(-1.84, -24.16) * mm});
            skLineSegment(sketch, "E540", {"start": v(-1.84, -24.16) * mm, "end": v(-0.95, -23.98) * mm});
            skLineSegment(sketch, "E541", {"start": v(-0.95, -23.98) * mm, "end": v(-0.1, -23.7) * mm});
            skLineSegment(sketch, "E542", {"start": v(-0.1, -23.7) * mm, "end": v(-0.07, -23.51) * mm});
            skLineSegment(sketch, "E543", {"start": v(-0.07, -23.51) * mm, "end": v(0, -22.7) * mm});
            skLineSegment(sketch, "E544", {"start": v(0, -22.7) * mm, "end": v(0, -22.07) * mm});
            skLineSegment(sketch, "E545", {"start": v(0, -22.07) * mm, "end": v(-0.05, -21.61) * mm});
            skLineSegment(sketch, "E546", {"start": v(-0.05, -21.61) * mm, "end": v(-0.1, -21.32) * mm});
            skLineSegment(sketch, "E547", {"start": v(-0.1, -21.32) * mm, "end": v(-0.12, -21.23) * mm});
            skLineSegment(sketch, "E548", {"start": v(-0.12, -21.23) * mm, "end": v(-0.26, -20.95) * mm});
            skLineSegment(sketch, "E549", {"start": v(-0.26, -20.95) * mm, "end": v(-0.42, -20.42) * mm});
            skLineSegment(sketch, "E550", {"start": v(-0.42, -20.42) * mm, "end": v(-0.45, -20.02) * mm});
            skLineSegment(sketch, "E551", {"start": v(-0.45, -20.02) * mm, "end": v(-0.38, -19.78) * mm});
            skLineSegment(sketch, "E552", {"start": v(-0.38, -19.78) * mm, "end": v(-0.22, -19.72) * mm});
            skLineSegment(sketch, "E553", {"start": v(-0.22, -19.72) * mm, "end": v(-0.2, -19.71) * mm});
            skLineSegment(sketch, "E554", {"start": v(-0.2, -19.71) * mm, "end": v(1.48, -19.01) * mm});
            skLineSegment(sketch, "E555", {"start": v(1.48, -19.01) * mm, "end": v(1.5, -19) * mm});
            skLineSegment(sketch, "E556", {"start": v(1.5, -19) * mm, "end": v(1.66, -18.94) * mm});
            skLineSegment(sketch, "E557", {"start": v(1.66, -18.94) * mm, "end": v(1.88, -19.06) * mm});
            skLineSegment(sketch, "E558", {"start": v(1.88, -19.06) * mm, "end": v(2.14, -19.36) * mm});
            skLineSegment(sketch, "E559", {"start": v(2.14, -19.36) * mm, "end": v(2.4, -19.85) * mm});
            skLineSegment(sketch, "E560", {"start": v(2.4, -19.85) * mm, "end": v(2.5, -20.14) * mm});
            skLineSegment(sketch, "E561", {"start": v(2.5, -20.14) * mm, "end": v(2.55, -20.23) * mm});
            skLineSegment(sketch, "E562", {"start": v(2.55, -20.23) * mm, "end": v(2.71, -20.47) * mm});
            skLineSegment(sketch, "E563", {"start": v(2.71, -20.47) * mm, "end": v(3.01, -20.83) * mm});
            skLineSegment(sketch, "E564", {"start": v(3.01, -20.83) * mm, "end": v(3.46, -21.28) * mm});
            skLineSegment(sketch, "E565", {"start": v(3.46, -21.28) * mm, "end": v(4.07, -21.8) * mm});
            skLineSegment(sketch, "E566", {"start": v(4.07, -21.8) * mm, "end": v(4.22, -21.9) * mm});
            skLineSegment(sketch, "E567", {"start": v(4.22, -21.9) * mm, "end": v(5.03, -21.5) * mm});
            skLineSegment(sketch, "E568", {"start": v(5.03, -21.5) * mm, "end": v(5.79, -21) * mm});
            skLineSegment(sketch, "E569", {"start": v(5.79, -21) * mm, "end": v(5.77, -20.82) * mm});
            skLineSegment(sketch, "E570", {"start": v(5.77, -20.82) * mm, "end": v(5.63, -20.02) * mm});
            skLineSegment(sketch, "E571", {"start": v(5.63, -20.02) * mm, "end": v(5.46, -19.41) * mm});
            skLineSegment(sketch, "E572", {"start": v(5.46, -19.41) * mm, "end": v(5.3, -18.98) * mm});
            skLineSegment(sketch, "E573", {"start": v(5.3, -18.98) * mm, "end": v(5.17, -18.71) * mm});
            skLineSegment(sketch, "E574", {"start": v(5.17, -18.71) * mm, "end": v(5.12, -18.63) * mm});
            skLineSegment(sketch, "E575", {"start": v(5.12, -18.63) * mm, "end": v(4.92, -18.4) * mm});
            skLineSegment(sketch, "E576", {"start": v(4.92, -18.4) * mm, "end": v(4.62, -17.92) * mm});
            skLineSegment(sketch, "E577", {"start": v(4.62, -17.92) * mm, "end": v(4.5, -17.55) * mm});
            skLineSegment(sketch, "E578", {"start": v(4.5, -17.55) * mm, "end": v(4.5, -17.3) * mm});
            skLineSegment(sketch, "E579", {"start": v(4.5, -17.3) * mm, "end": v(4.64, -17.2) * mm});
            skLineSegment(sketch, "E580", {"start": v(4.64, -17.2) * mm, "end": v(4.65, -17.18) * mm});
            skLineSegment(sketch, "E581", {"start": v(4.65, -17.18) * mm, "end": v(6.1, -16.07) * mm});
            skLineSegment(sketch, "E582", {"start": v(6.1, -16.07) * mm, "end": v(6.12, -16.06) * mm});
            skLineSegment(sketch, "E583", {"start": v(6.12, -16.06) * mm, "end": v(6.25, -15.96) * mm});
            skLineSegment(sketch, "E584", {"start": v(6.25, -15.96) * mm, "end": v(6.5, -16) * mm});
            skLineSegment(sketch, "E585", {"start": v(6.5, -16) * mm, "end": v(6.82, -16.23) * mm});
            skLineSegment(sketch, "E586", {"start": v(6.82, -16.23) * mm, "end": v(7.2, -16.65) * mm});
            skLineSegment(sketch, "E587", {"start": v(7.2, -16.65) * mm, "end": v(7.38, -16.9) * mm});
            skLineSegment(sketch, "E588", {"start": v(7.38, -16.9) * mm, "end": v(7.44, -16.97) * mm});
            skLineSegment(sketch, "E589", {"start": v(7.44, -16.97) * mm, "end": v(7.67, -17.16) * mm});
            skLineSegment(sketch, "E590", {"start": v(7.67, -17.16) * mm, "end": v(8.05, -17.43) * mm});
            skLineSegment(sketch, "E591", {"start": v(8.05, -17.43) * mm, "end": v(8.6, -17.75) * mm});
            skLineSegment(sketch, "E592", {"start": v(8.6, -17.75) * mm, "end": v(9.32, -18.1) * mm});
            skLineSegment(sketch, "E593", {"start": v(9.32, -18.1) * mm, "end": v(9.5, -18.15) * mm});
            skLineSegment(sketch, "E594", {"start": v(9.5, -18.15) * mm, "end": v(10.18, -17.56) * mm});
            skLineSegment(sketch, "E595", {"start": v(10.18, -17.56) * mm, "end": v(10.77, -16.88) * mm});
            skLineSegment(sketch, "E596", {"start": v(10.77, -16.88) * mm, "end": v(10.7, -16.7) * mm});
            skLineSegment(sketch, "E597", {"start": v(10.7, -16.7) * mm, "end": v(10.37, -15.98) * mm});
            skLineSegment(sketch, "E598", {"start": v(10.37, -15.98) * mm, "end": v(10.05, -15.43) * mm});
            skLineSegment(sketch, "E599", {"start": v(10.05, -15.43) * mm, "end": v(9.78, -15.05) * mm});
            skLineSegment(sketch, "E600", {"start": v(9.78, -15.05) * mm, "end": v(9.59, -14.83) * mm});
            skLineSegment(sketch, "E601", {"start": v(9.59, -14.83) * mm, "end": v(9.52, -14.76) * mm});
            skLineSegment(sketch, "E602", {"start": v(9.52, -14.76) * mm, "end": v(9.26, -14.58) * mm});
            skLineSegment(sketch, "E603", {"start": v(9.26, -14.58) * mm, "end": v(8.85, -14.2) * mm});
            skLineSegment(sketch, "E604", {"start": v(8.85, -14.2) * mm, "end": v(8.63, -13.88) * mm});
            skLineSegment(sketch, "E605", {"start": v(8.63, -13.88) * mm, "end": v(8.58, -13.63) * mm});
            skLineSegment(sketch, "E606", {"start": v(8.58, -13.63) * mm, "end": v(8.68, -13.5) * mm});
            skLineSegment(sketch, "E607", {"start": v(8.68, -13.5) * mm, "end": v(8.69, -13.48) * mm});
            skLineSegment(sketch, "E608", {"start": v(8.69, -13.48) * mm, "end": v(9.8, -12.03) * mm});
            skLineSegment(sketch, "E609", {"start": v(9.8, -12.03) * mm, "end": v(9.81, -12.02) * mm});
            skLineSegment(sketch, "E610", {"start": v(9.81, -12.02) * mm, "end": v(9.92, -11.88) * mm});
            skLineSegment(sketch, "E611", {"start": v(9.92, -11.88) * mm, "end": v(10.17, -11.87) * mm});
            skLineSegment(sketch, "E612", {"start": v(10.17, -11.87) * mm, "end": v(10.54, -12) * mm});
            skLineSegment(sketch, "E613", {"start": v(10.54, -12) * mm, "end": v(11.01, -12.3) * mm});
            skLineSegment(sketch, "E614", {"start": v(11.01, -12.3) * mm, "end": v(11.25, -12.5) * mm});
            skLineSegment(sketch, "E615", {"start": v(11.25, -12.5) * mm, "end": v(11.33, -12.55) * mm});
            skLineSegment(sketch, "E616", {"start": v(11.33, -12.55) * mm, "end": v(11.6, -12.68) * mm});
            skLineSegment(sketch, "E617", {"start": v(11.6, -12.68) * mm, "end": v(12.03, -12.84) * mm});
            skLineSegment(sketch, "E618", {"start": v(12.03, -12.84) * mm, "end": v(12.64, -13) * mm});
            skLineSegment(sketch, "E619", {"start": v(12.64, -13) * mm, "end": v(13.44, -13.15) * mm});
            skLineSegment(sketch, "E620", {"start": v(13.44, -13.15) * mm, "end": v(13.62, -13.17) * mm});
            skLineSegment(sketch, "E621", {"start": v(13.62, -13.17) * mm, "end": v(14.12, -12.41) * mm});
            skLineSegment(sketch, "E622", {"start": v(14.12, -12.41) * mm, "end": v(14.52, -11.6) * mm});
            skLineSegment(sketch, "E623", {"start": v(14.52, -11.6) * mm, "end": v(14.42, -11.45) * mm});
            skLineSegment(sketch, "E624", {"start": v(14.42, -11.45) * mm, "end": v(13.9, -10.84) * mm});
            skLineSegment(sketch, "E625", {"start": v(13.9, -10.84) * mm, "end": v(13.44, -10.4) * mm});
            skLineSegment(sketch, "E626", {"start": v(13.44, -10.4) * mm, "end": v(13.09, -10.1) * mm});
            skLineSegment(sketch, "E627", {"start": v(13.09, -10.1) * mm, "end": v(12.85, -9.93) * mm});
            skLineSegment(sketch, "E628", {"start": v(12.85, -9.93) * mm, "end": v(12.76, -9.88) * mm});
            skLineSegment(sketch, "E629", {"start": v(12.76, -9.88) * mm, "end": v(12.47, -9.78) * mm});
            skLineSegment(sketch, "E630", {"start": v(12.47, -9.78) * mm, "end": v(11.98, -9.52) * mm});
            skLineSegment(sketch, "E631", {"start": v(11.98, -9.52) * mm, "end": v(11.67, -9.26) * mm});
            skLineSegment(sketch, "E632", {"start": v(11.67, -9.26) * mm, "end": v(11.56, -9.04) * mm});
            skLineSegment(sketch, "E633", {"start": v(11.56, -9.04) * mm, "end": v(11.62, -8.88) * mm});
            skLineSegment(sketch, "E634", {"start": v(11.62, -8.88) * mm, "end": v(11.63, -8.87) * mm});
            skLineSegment(sketch, "E635", {"start": v(11.63, -8.87) * mm, "end": v(12.33, -7.18) * mm});
            skLineSegment(sketch, "E636", {"start": v(12.33, -7.18) * mm, "end": v(12.34, -7.16) * mm});
            skLineSegment(sketch, "E637", {"start": v(12.34, -7.16) * mm, "end": v(12.4, -7) * mm});
            skLineSegment(sketch, "E638", {"start": v(12.4, -7) * mm, "end": v(12.64, -6.93) * mm});
            skLineSegment(sketch, "E639", {"start": v(12.64, -6.93) * mm, "end": v(13.04, -6.96) * mm});
            skLineSegment(sketch, "E640", {"start": v(13.04, -6.96) * mm, "end": v(13.57, -7.12) * mm});
            skLineSegment(sketch, "E641", {"start": v(13.57, -7.12) * mm, "end": v(13.85, -7.26) * mm});
            skLineSegment(sketch, "E642", {"start": v(13.85, -7.26) * mm, "end": v(13.94, -7.28) * mm});
            skLineSegment(sketch, "E643", {"start": v(13.94, -7.28) * mm, "end": v(14.23, -7.33) * mm});
            skLineSegment(sketch, "E644", {"start": v(14.23, -7.33) * mm, "end": v(14.7, -7.38) * mm});
            skLineSegment(sketch, "E645", {"start": v(14.7, -7.38) * mm, "end": v(15.33, -7.38) * mm});
            skLineSegment(sketch, "E646", {"start": v(15.33, -7.38) * mm, "end": v(16.13, -7.31) * mm});
            skLineSegment(sketch, "E647", {"start": v(16.13, -7.31) * mm, "end": v(16.31, -7.28) * mm});
            skLineSegment(sketch, "E648", {"start": v(14.7, 4.3) * mm, "end": v(14.35, 3.65) * mm});
            skLineSegment(sketch, "E649", {"start": v(14.35, 3.65) * mm, "end": v(14.14, 2.96) * mm});
            skLineSegment(sketch, "E650", {"start": v(14.14, 2.96) * mm, "end": v(14.48, 2.44) * mm});
            skLineSegment(sketch, "E651", {"start": v(14.48, 2.44) * mm, "end": v(15.27, 1.73) * mm});
            skLineSegment(sketch, "E652", {"start": v(15.27, 1.73) * mm, "end": v(15.62, 1.55) * mm});
            skLineSegment(sketch, "E653", {"start": v(15.62, 1.55) * mm, "end": v(15.7, 1.58) * mm});
            skLineSegment(sketch, "E654", {"start": v(15.7, 1.58) * mm, "end": v(15.77, 1.48) * mm});
            skLineSegment(sketch, "E655", {"start": v(15.77, 1.48) * mm, "end": v(15.78, 1.47) * mm});
            skLineSegment(sketch, "E656", {"start": v(15.78, 1.47) * mm, "end": v(16.89, 1.53) * mm});
            skLineSegment(sketch, "E657", {"start": v(16.89, 1.53) * mm, "end": v(17.5, 1.1) * mm});
            skLineSegment(sketch, "E658", {"start": v(17.5, 1.1) * mm, "end": v(17.5, -1.1) * mm});
            skLineSegment(sketch, "E659", {"start": v(17.5, -1.1) * mm, "end": v(16.89, -1.53) * mm});
            skLineSegment(sketch, "E660", {"start": v(16.89, -1.53) * mm, "end": v(15.78, -1.47) * mm});
            skLineSegment(sketch, "E661", {"start": v(15.78, -1.47) * mm, "end": v(15.77, -1.48) * mm});
            skLineSegment(sketch, "E662", {"start": v(15.77, -1.48) * mm, "end": v(15.7, -1.58) * mm});
            skLineSegment(sketch, "E663", {"start": v(15.7, -1.58) * mm, "end": v(15.62, -1.55) * mm});
            skLineSegment(sketch, "E664", {"start": v(15.62, -1.55) * mm, "end": v(15.27, -1.73) * mm});
            skLineSegment(sketch, "E665", {"start": v(15.27, -1.73) * mm, "end": v(14.48, -2.44) * mm});
            skLineSegment(sketch, "E666", {"start": v(14.48, -2.44) * mm, "end": v(14.14, -2.96) * mm});
            skLineSegment(sketch, "E667", {"start": v(14.14, -2.96) * mm, "end": v(14.35, -3.65) * mm});
            skLineSegment(sketch, "E668", {"start": v(14.35, -3.65) * mm, "end": v(14.7, -4.3) * mm});
            skLineSegment(sketch, "E669", {"start": v(14.7, -4.3) * mm, "end": v(15.3, -4.42) * mm});
            skLineSegment(sketch, "E670", {"start": v(15.3, -4.42) * mm, "end": v(16.36, -4.37) * mm});
            skLineSegment(sketch, "E671", {"start": v(16.36, -4.37) * mm, "end": v(16.74, -4.25) * mm});
            skLineSegment(sketch, "E672", {"start": v(16.74, -4.25) * mm, "end": v(16.78, -4.17) * mm});
            skLineSegment(sketch, "E673", {"start": v(16.98, -3.42) * mm, "end": v(17.1, -3.45) * mm});
            skLineSegment(sketch, "E674", {"start": v(16.9, -4.2) * mm, "end": v(16.9, -4.19) * mm});
            skLineSegment(sketch, "E675", {"start": v(16.9, -4.19) * mm, "end": v(17.65, -3.37) * mm});
            skLineSegment(sketch, "E676", {"start": v(17.65, -3.37) * mm, "end": v(18.38, -3.24) * mm});
            skLineSegment(sketch, "E677", {"start": v(18.38, -3.24) * mm, "end": v(19.94, -4.8) * mm});
            skLineSegment(sketch, "E678", {"start": v(19.94, -4.8) * mm, "end": v(19.8, -5.53) * mm});
            skLineSegment(sketch, "E679", {"start": v(19.8, -5.53) * mm, "end": v(19, -6.27) * mm});
            skLineSegment(sketch, "E680", {"start": v(19, -6.27) * mm, "end": v(18.98, -6.28) * mm});
            skLineSegment(sketch, "E681", {"start": v(18.98, -6.28) * mm, "end": v(19.01, -6.4) * mm});
            skLineSegment(sketch, "E682", {"start": v(19.01, -6.4) * mm, "end": v(18.93, -6.44) * mm});
            skLineSegment(sketch, "E683", {"start": v(18.93, -6.44) * mm, "end": v(18.8, -6.82) * mm});
            skLineSegment(sketch, "E684", {"start": v(18.8, -6.82) * mm, "end": v(18.75, -7.88) * mm});
            skLineSegment(sketch, "E685", {"start": v(18.75, -7.88) * mm, "end": v(18.88, -8.48) * mm});
            skLineSegment(sketch, "E686", {"start": v(18.88, -8.48) * mm, "end": v(19.52, -8.82) * mm});
            skLineSegment(sketch, "E687", {"start": v(19.52, -8.82) * mm, "end": v(20.21, -9.03) * mm});
            skLineSegment(sketch, "E688", {"start": v(20.21, -9.03) * mm, "end": v(20.73, -8.7) * mm});
            skLineSegment(sketch, "E689", {"start": v(20.73, -8.7) * mm, "end": v(21.45, -7.91) * mm});
            skLineSegment(sketch, "E690", {"start": v(21.45, -7.91) * mm, "end": v(21.63, -7.56) * mm});
            skLineSegment(sketch, "E691", {"start": v(21.63, -7.56) * mm, "end": v(21.6, -7.47) * mm});
            skLineSegment(sketch, "E692", {"start": v(21.6, -7.47) * mm, "end": v(21.7, -7.41) * mm});
            skLineSegment(sketch, "E693", {"start": v(21.7, -7.41) * mm, "end": v(21.7, -7.4) * mm});
            skLineSegment(sketch, "E694", {"start": v(21.7, -7.4) * mm, "end": v(21.65, -6.29) * mm});
            skLineSegment(sketch, "E695", {"start": v(21.65, -6.29) * mm, "end": v(22.08, -5.68) * mm});
            skLineSegment(sketch, "E696", {"start": v(22.08, -5.68) * mm, "end": v(24.28, -5.68) * mm});
            skLineSegment(sketch, "E697", {"start": v(24.28, -5.68) * mm, "end": v(24.7, -6.29) * mm});
            skLineSegment(sketch, "E698", {"start": v(24.7, -6.29) * mm, "end": v(24.65, -7.4) * mm});
            skLineSegment(sketch, "E699", {"start": v(24.65, -7.4) * mm, "end": v(24.65, -7.41) * mm});
            skLineSegment(sketch, "E700", {"start": v(24.65, -7.41) * mm, "end": v(24.75, -7.47) * mm});
            skLineSegment(sketch, "E701", {"start": v(24.75, -7.47) * mm, "end": v(24.73, -7.56) * mm});
            skLineSegment(sketch, "E702", {"start": v(24.73, -7.56) * mm, "end": v(24.9, -7.91) * mm});
            skLineSegment(sketch, "E703", {"start": v(24.9, -7.91) * mm, "end": v(25.62, -8.7) * mm});
            skLineSegment(sketch, "E704", {"start": v(25.62, -8.7) * mm, "end": v(26.14, -9.03) * mm});
            skLineSegment(sketch, "E705", {"start": v(26.14, -9.03) * mm, "end": v(26.83, -8.82) * mm});
            skLineSegment(sketch, "E706", {"start": v(26.83, -8.82) * mm, "end": v(27.47, -8.48) * mm});
            skLineSegment(sketch, "E707", {"start": v(27.47, -8.48) * mm, "end": v(27.6, -7.88) * mm});
            skLineSegment(sketch, "E708", {"start": v(27.6, -7.88) * mm, "end": v(27.55, -6.82) * mm});
            skLineSegment(sketch, "E709", {"start": v(27.55, -6.82) * mm, "end": v(27.43, -6.44) * mm});
            skLineSegment(sketch, "E710", {"start": v(27.43, -6.44) * mm, "end": v(27.34, -6.4) * mm});
            skLineSegment(sketch, "E711", {"start": v(27.34, -6.4) * mm, "end": v(27.37, -6.28) * mm});
            skLineSegment(sketch, "E712", {"start": v(27.37, -6.28) * mm, "end": v(27.36, -6.27) * mm});
            skLineSegment(sketch, "E713", {"start": v(27.36, -6.27) * mm, "end": v(26.54, -5.53) * mm});
            skLineSegment(sketch, "E714", {"start": v(26.54, -5.53) * mm, "end": v(26.41, -4.8) * mm});
            skLineSegment(sketch, "E715", {"start": v(26.41, -4.8) * mm, "end": v(27.97, -3.24) * mm});
            skLineSegment(sketch, "E716", {"start": v(27.97, -3.24) * mm, "end": v(28.7, -3.37) * mm});
            skLineSegment(sketch, "E717", {"start": v(28.7, -3.37) * mm, "end": v(29.44, -4.19) * mm});
            skLineSegment(sketch, "E718", {"start": v(29.44, -4.19) * mm, "end": v(29.46, -4.2) * mm});
            skLineSegment(sketch, "E719", {"start": v(29.46, -4.2) * mm, "end": v(29.57, -4.17) * mm});
            skLineSegment(sketch, "E720", {"start": v(29.57, -4.17) * mm, "end": v(29.62, -4.25) * mm});
            skLineSegment(sketch, "E721", {"start": v(29.62, -4.25) * mm, "end": v(30, -4.37) * mm});
            skLineSegment(sketch, "E722", {"start": v(30, -4.37) * mm, "end": v(31.05, -4.42) * mm});
            skLineSegment(sketch, "E723", {"start": v(31.05, -4.42) * mm, "end": v(31.66, -4.3) * mm});
            skLineSegment(sketch, "E724", {"start": v(31.66, -4.3) * mm, "end": v(32, -3.65) * mm});
            skLineSegment(sketch, "E725", {"start": v(32, -3.65) * mm, "end": v(32.2, -2.96) * mm});
            skLineSegment(sketch, "E726", {"start": v(32.2, -2.96) * mm, "end": v(31.87, -2.44) * mm});
            skLineSegment(sketch, "E727", {"start": v(31.87, -2.44) * mm, "end": v(31.09, -1.73) * mm});
            skLineSegment(sketch, "E728", {"start": v(31.09, -1.73) * mm, "end": v(30.74, -1.55) * mm});
            skLineSegment(sketch, "E729", {"start": v(30.74, -1.55) * mm, "end": v(30.65, -1.58) * mm});
            skLineSegment(sketch, "E730", {"start": v(30.65, -1.58) * mm, "end": v(30.59, -1.48) * mm});
            skLineSegment(sketch, "E731", {"start": v(30.59, -1.48) * mm, "end": v(30.57, -1.47) * mm});
            skLineSegment(sketch, "E732", {"start": v(30.57, -1.47) * mm, "end": v(29.47, -1.53) * mm});
            skLineSegment(sketch, "E733", {"start": v(29.47, -1.53) * mm, "end": v(28.86, -1.1) * mm});
            skLineSegment(sketch, "E734", {"start": v(28.86, -1.1) * mm, "end": v(28.86, 1.1) * mm});
            skLineSegment(sketch, "E735", {"start": v(28.86, 1.1) * mm, "end": v(29.47, 1.53) * mm});
            skLineSegment(sketch, "E736", {"start": v(29.47, 1.53) * mm, "end": v(30.57, 1.47) * mm});
            skLineSegment(sketch, "E737", {"start": v(30.57, 1.47) * mm, "end": v(30.59, 1.48) * mm});
            skLineSegment(sketch, "E738", {"start": v(30.59, 1.48) * mm, "end": v(30.65, 1.58) * mm});
            skLineSegment(sketch, "E739", {"start": v(30.65, 1.58) * mm, "end": v(30.74, 1.55) * mm});
            skLineSegment(sketch, "E740", {"start": v(30.74, 1.55) * mm, "end": v(31.09, 1.73) * mm});
            skLineSegment(sketch, "E741", {"start": v(31.09, 1.73) * mm, "end": v(31.87, 2.44) * mm});
            skLineSegment(sketch, "E742", {"start": v(31.87, 2.44) * mm, "end": v(32.2, 2.96) * mm});
            skLineSegment(sketch, "E743", {"start": v(32.2, 2.96) * mm, "end": v(32, 3.65) * mm});
            skLineSegment(sketch, "E744", {"start": v(32, 3.65) * mm, "end": v(31.66, 4.3) * mm});
            skLineSegment(sketch, "E745", {"start": v(31.66, 4.3) * mm, "end": v(31.05, 4.42) * mm});
            skLineSegment(sketch, "E746", {"start": v(31.05, 4.42) * mm, "end": v(30, 4.37) * mm});
            skLineSegment(sketch, "E747", {"start": v(30, 4.37) * mm, "end": v(29.62, 4.25) * mm});
            skLineSegment(sketch, "E748", {"start": v(29.62, 4.25) * mm, "end": v(29.57, 4.17) * mm});
            skLineSegment(sketch, "E749", {"start": v(29.57, 4.17) * mm, "end": v(29.46, 4.2) * mm});
            skLineSegment(sketch, "E750", {"start": v(29.46, 4.2) * mm, "end": v(29.44, 4.19) * mm});
            skLineSegment(sketch, "E751", {"start": v(29.44, 4.19) * mm, "end": v(28.7, 3.37) * mm});
            skLineSegment(sketch, "E752", {"start": v(28.7, 3.37) * mm, "end": v(27.97, 3.24) * mm});
            skLineSegment(sketch, "E753", {"start": v(27.97, 3.24) * mm, "end": v(26.41, 4.8) * mm});
            skLineSegment(sketch, "E754", {"start": v(26.41, 4.8) * mm, "end": v(26.54, 5.53) * mm});
            skLineSegment(sketch, "E755", {"start": v(26.54, 5.53) * mm, "end": v(27.36, 6.27) * mm});
            skLineSegment(sketch, "E756", {"start": v(27.36, 6.27) * mm, "end": v(27.37, 6.28) * mm});
            skLineSegment(sketch, "E757", {"start": v(27.37, 6.28) * mm, "end": v(27.34, 6.4) * mm});
            skLineSegment(sketch, "E758", {"start": v(27.34, 6.4) * mm, "end": v(27.43, 6.44) * mm});
            skLineSegment(sketch, "E759", {"start": v(27.43, 6.44) * mm, "end": v(27.55, 6.82) * mm});
            skLineSegment(sketch, "E760", {"start": v(27.55, 6.82) * mm, "end": v(27.6, 7.88) * mm});
            skLineSegment(sketch, "E761", {"start": v(27.6, 7.88) * mm, "end": v(27.47, 8.48) * mm});
            skLineSegment(sketch, "E762", {"start": v(27.47, 8.48) * mm, "end": v(26.83, 8.82) * mm});
            skLineSegment(sketch, "E763", {"start": v(26.83, 8.82) * mm, "end": v(26.14, 9.03) * mm});
            skLineSegment(sketch, "E764", {"start": v(26.14, 9.03) * mm, "end": v(25.62, 8.7) * mm});
            skLineSegment(sketch, "E765", {"start": v(25.62, 8.7) * mm, "end": v(24.9, 7.91) * mm});
            skLineSegment(sketch, "E766", {"start": v(24.9, 7.91) * mm, "end": v(24.73, 7.56) * mm});
            skLineSegment(sketch, "E767", {"start": v(24.73, 7.56) * mm, "end": v(24.75, 7.47) * mm});
            skLineSegment(sketch, "E768", {"start": v(24.75, 7.47) * mm, "end": v(24.65, 7.41) * mm});
            skLineSegment(sketch, "E769", {"start": v(24.65, 7.41) * mm, "end": v(24.65, 7.4) * mm});
            skLineSegment(sketch, "E770", {"start": v(24.65, 7.4) * mm, "end": v(24.7, 6.29) * mm});
            skLineSegment(sketch, "E771", {"start": v(24.7, 6.29) * mm, "end": v(24.28, 5.68) * mm});
            skLineSegment(sketch, "E772", {"start": v(24.28, 5.68) * mm, "end": v(22.08, 5.68) * mm});
            skLineSegment(sketch, "E773", {"start": v(22.08, 5.68) * mm, "end": v(21.65, 6.29) * mm});
            skLineSegment(sketch, "E774", {"start": v(21.65, 6.29) * mm, "end": v(21.7, 7.4) * mm});
            skLineSegment(sketch, "E775", {"start": v(21.7, 7.4) * mm, "end": v(21.7, 7.41) * mm});
            skLineSegment(sketch, "E776", {"start": v(21.7, 7.41) * mm, "end": v(21.6, 7.47) * mm});
            skLineSegment(sketch, "E777", {"start": v(21.6, 7.47) * mm, "end": v(21.63, 7.56) * mm});
            skLineSegment(sketch, "E778", {"start": v(21.63, 7.56) * mm, "end": v(21.45, 7.91) * mm});
            skLineSegment(sketch, "E779", {"start": v(21.45, 7.91) * mm, "end": v(20.73, 8.7) * mm});
            skLineSegment(sketch, "E780", {"start": v(20.73, 8.7) * mm, "end": v(20.21, 9.03) * mm});
            skLineSegment(sketch, "E781", {"start": v(20.21, 9.03) * mm, "end": v(19.52, 8.82) * mm});
            skLineSegment(sketch, "E782", {"start": v(19.52, 8.82) * mm, "end": v(18.88, 8.48) * mm});
            skLineSegment(sketch, "E783", {"start": v(18.88, 8.48) * mm, "end": v(18.75, 7.88) * mm});
            skLineSegment(sketch, "E784", {"start": v(18.75, 7.88) * mm, "end": v(18.8, 6.82) * mm});
            skLineSegment(sketch, "E785", {"start": v(18.8, 6.82) * mm, "end": v(18.93, 6.44) * mm});
            skLineSegment(sketch, "E786", {"start": v(18.93, 6.44) * mm, "end": v(19.01, 6.4) * mm});
            skLineSegment(sketch, "E787", {"start": v(19.01, 6.4) * mm, "end": v(18.98, 6.28) * mm});
            skLineSegment(sketch, "E788", {"start": v(18.98, 6.28) * mm, "end": v(19, 6.27) * mm});
            skLineSegment(sketch, "E789", {"start": v(19, 6.27) * mm, "end": v(19.8, 5.53) * mm});
            skLineSegment(sketch, "E790", {"start": v(19.8, 5.53) * mm, "end": v(19.94, 4.8) * mm});
            skLineSegment(sketch, "E791", {"start": v(19.94, 4.8) * mm, "end": v(18.38, 3.24) * mm});
            skLineSegment(sketch, "E792", {"start": v(18.38, 3.24) * mm, "end": v(17.65, 3.37) * mm});
            skLineSegment(sketch, "E793", {"start": v(17.65, 3.37) * mm, "end": v(16.9, 4.19) * mm});
            skLineSegment(sketch, "E794", {"start": v(16.9, 4.19) * mm, "end": v(16.9, 4.2) * mm});
            skLineSegment(sketch, "E795", {"start": v(16.9, 4.2) * mm, "end": v(16.78, 4.17) * mm});
            skLineSegment(sketch, "E796", {"start": v(16.78, 4.17) * mm, "end": v(16.74, 4.25) * mm});
            skLineSegment(sketch, "E797", {"start": v(16.74, 4.25) * mm, "end": v(16.36, 4.37) * mm});
            skLineSegment(sketch, "E798", {"start": v(16.36, 4.37) * mm, "end": v(15.3, 4.42) * mm});
            skLineSegment(sketch, "E799", {"start": v(15.3, 4.42) * mm, "end": v(14.7, 4.3) * mm});
            skCircle(sketch, "E800", {"center": v(-7.38, 0) * mm, "radius": 24.83 * mm, "construction": true});
            skCircle(sketch, "E801", {"center": v(23.18, 0) * mm, "radius": 9.55 * mm, "construction": true});
            skCircle(sketch, "E802", {"center": v(23.18, 0) * mm, "radius": 1.15 * mm});
            skCircle(sketch, "E803.cCircle", {"center": v(-7.38, 0) * mm, "radius": 5 * mm, "construction": true});
            skLineSegment(sketch, "E803.0", {"start": v(-4.5, 5) * mm, "end": v(-1.6, 0) * mm});
            skLineSegment(sketch, "E803.1", {"start": v(-1.6, 0) * mm, "end": v(-4.5, -5) * mm});
            skLineSegment(sketch, "E803.2", {"start": v(-4.5, -5) * mm, "end": v(-10.27, -5) * mm});
            skLineSegment(sketch, "E803.3", {"start": v(-10.27, -5) * mm, "end": v(-13.15, 0) * mm});
            skLineSegment(sketch, "E803.4", {"start": v(-13.15, 0) * mm, "end": v(-10.27, 5) * mm});
            skLineSegment(sketch, "E803.5", {"start": v(-10.27, 5) * mm, "end": v(-4.5, 5) * mm});
            skPoint(sketch, "E803.0.midPoint", {"position": v(-3.05, 2.5) * mm});
            skCircle(sketch, "E804", {"center": v(-7.38, 0) * mm, "radius": 3 * mm});
            skSolve(sketch);
        }
        {
            var Q0;
            Q0=makeQuery(id+"F0.imprint","IMPRINT",FACE,{"disambiguationData":[TD([[makeQuery(id+"F0.imprint","IMPRINT",EDGE,{"derivedFrom":sQuery(id+"F0.wireOp",EDGE,"E0")}),1.0]])]});
            var Q1;
            Q1=makeQuery(id+"F0.imprint","IMPRINT",FACE,{"disambiguationData":[TD([[makeQuery(id+"F0.imprint","IMPRINT",EDGE,{"derivedFrom":sQuery(id+"F0.wireOp",EDGE,"E803.0")}),-1.0]])]});
            extrude(context, id + "F1", {"entities" : qUnion([Q0, Q1]), "depth" : 2 * mm});
        }
        {
            var Q0;
            Q0=makeQuery(id+"F0.imprint","IMPRINT",FACE,{"disambiguationData":[TD([[makeQuery(id+"F0.imprint","IMPRINT",EDGE,{"derivedFrom":sQuery(id+"F0.wireOp",EDGE,"E0")}),1.0]])]});
            extrude(context, id + "F2", {"entities" : qUnion([Q0]), "operationType" : NewBodyOperationType.ADD, "oppositeDirection" : true, "depth" : 3 * mm});
        }
    });
